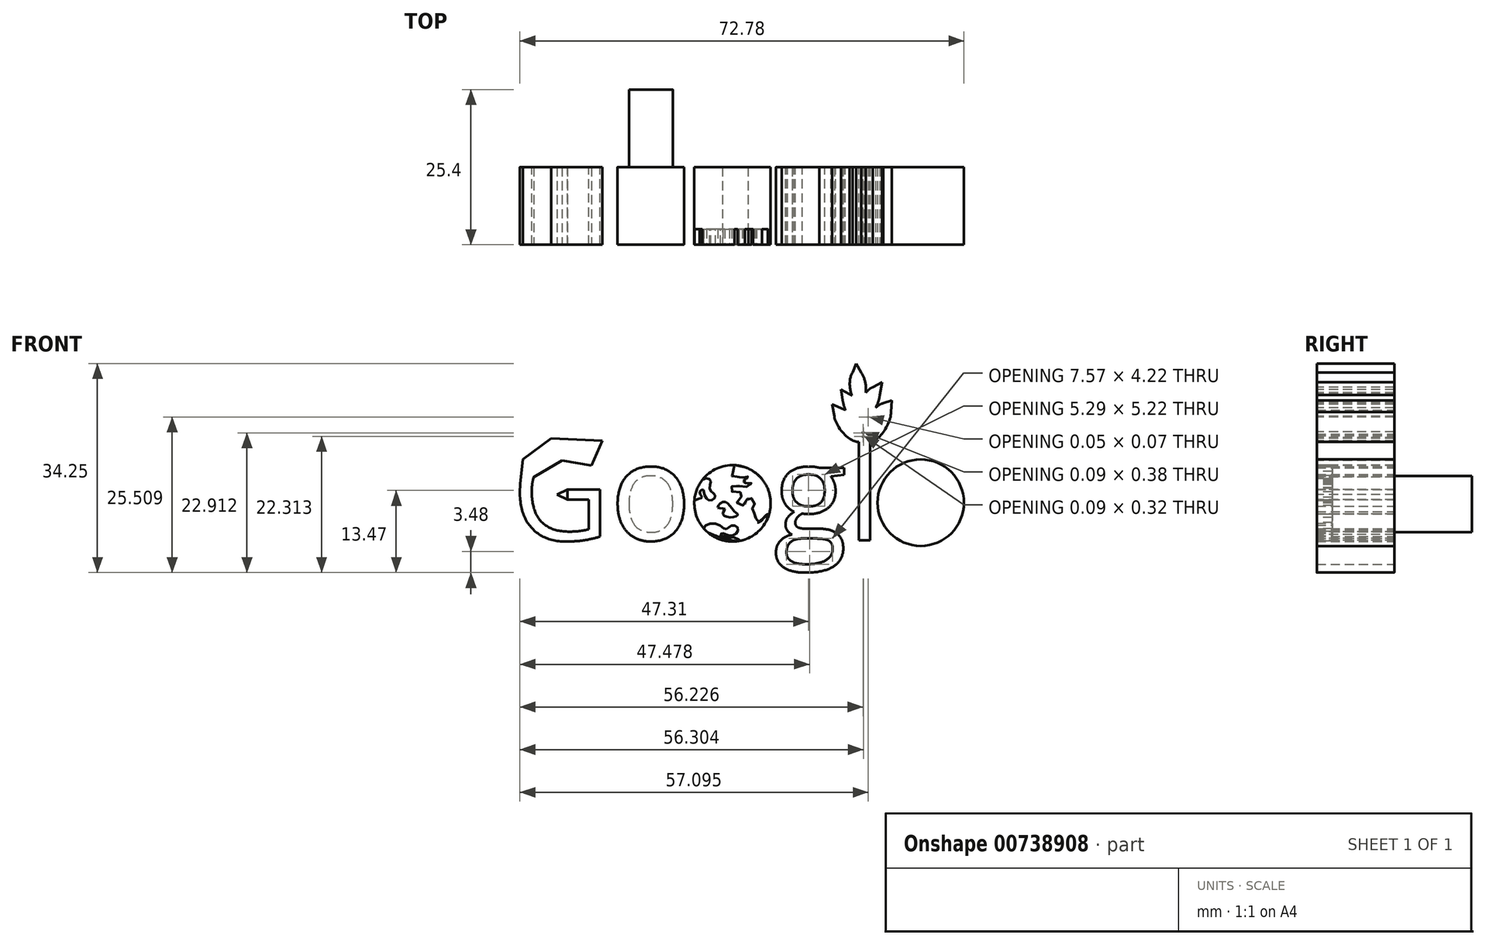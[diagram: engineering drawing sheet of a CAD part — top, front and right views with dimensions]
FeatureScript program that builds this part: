
annotation { "Feature Type Name" : "Feature", "Feature Type Description" : "" }
export const myFeature = defineFeature(function(context is Context, id is Id, definition is map)
    precondition{}
    {
        {
            var Q0;
            Q0=qCreatedBy(makeId("Front.planeOp"),FACE);
            var sketch = newSketch(context, id + "F0", { "sketchPlane" : qUnion([Q0])});
            skText(sketch, "E0", { "text": "Google", "fontName": "OpenSans-Regular.ttf"});
            const initialGuessF0  = {"E0": [-0.08015, -0.00937, 1, 0, 0.01595]};
            skSetInitialGuess(sketch, initialGuessF0);
            skSolve(sketch);
        }
        {
            var Q0;
            Q0 = qSketchRegion(id + "F0", true);
            extrude(context, id + "F1", {"entities" : qUnion([Q0]), "depth" : 12.7 * mm, "offsetDistance" : 25.4 * mm});
        }
        {
            var Q0;
            Q0=makeQuery(id+"F1.opExtrude","CAP_FACE",FACE,{"disambiguationData":[OSD([sQuery(id+"F0.wireOp",EDGE,"E0.sketch_text.stroke-0"),sQuery(id+"F0.wireOp",EDGE,"E0.sketch_text.stroke-1"),sQuery(id+"F0.wireOp",EDGE,"E0.sketch_text.stroke-2"),sQuery(id+"F0.wireOp",EDGE,"E0.sketch_text.stroke-3"),sQuery(id+"F0.wireOp",EDGE,"E0.sketch_text.stroke-4"),sQuery(id+"F0.wireOp",EDGE,"E0.sketch_text.stroke-5"),sQuery(id+"F0.wireOp",EDGE,"E0.sketch_text.stroke-6"),sQuery(id+"F0.wireOp",EDGE,"E0.sketch_text.stroke-7"),sQuery(id+"F0.wireOp",EDGE,"E0.sketch_text.stroke-8"),sQuery(id+"F0.wireOp",EDGE,"E0.sketch_text.stroke-9"),sQuery(id+"F0.wireOp",EDGE,"E0.sketch_text.stroke-10"),sQuery(id+"F0.wireOp",EDGE,"E0.sketch_text.stroke-11"),sQuery(id+"F0.wireOp",EDGE,"E0.sketch_text.stroke-12"),sQuery(id+"F0.wireOp",EDGE,"E0.sketch_text.stroke-13"),sQuery(id+"F0.wireOp",EDGE,"E0.sketch_text.stroke-14"),sQuery(id+"F0.wireOp",EDGE,"E0.sketch_text.stroke-15"),sQuery(id+"F0.wireOp",EDGE,"E0.sketch_text.stroke-16"),sQuery(id+"F0.wireOp",EDGE,"E0.sketch_text.stroke-17"),sQuery(id+"F0.wireOp",EDGE,"E0.sketch_text.stroke-18"),sQuery(id+"F0.wireOp",EDGE,"E0.sketch_text.stroke-19")])],"isStart":false});
            var sketch = newSketch(context, id + "F2", { "sketchPlane" : qUnion([Q0])});
            skLineSegment(sketch, "E1", {"start": v(-65.28, 6.96) * mm, "end": v(-67.07, 2.87) * mm});
            skLineSegment(sketch, "E2", {"start": v(-67.07, 2.87) * mm, "end": v(-74.25, 4.11) * mm});
            skLineSegment(sketch, "E3", {"start": v(-74.25, 4.11) * mm, "end": v(-67.07, 2.87) * mm});
            skLineSegment(sketch, "E4", {"start": v(-65.28, 6.96) * mm, "end": v(-73.65, 7.3) * mm});
            skLineSegment(sketch, "E5", {"start": v(-73.65, 7.3) * mm, "end": v(-78.28, 3.85) * mm});
            skLineSegment(sketch, "E6", {"start": v(-78.28, 3.85) * mm, "end": v(-78.74, -0.3) * mm});
            skLineSegment(sketch, "E7", {"start": v(-78.74, -0.3) * mm, "end": v(-71.88, 3.7) * mm});
            skSolve(sketch);
        }
        {
            var Q0;
            {var subQ5=sQuery(id+"F2.wireOp",EDGE,"E1");Q0=makeQuery(id+"F2.imprint","IMPRINT",FACE,{"disambiguationData":[TD([[makeQuery(id+"F2.imprint","IMPRINT",EDGE,{"derivedFrom":subQ5}),-1.0]])]});}
            extrude(context, id + "F3", {"entities" : qUnion([Q0]), "operationType" : NewBodyOperationType.ADD, "oppositeDirection" : true, "depth" : 12.7 * mm, "offsetDistance" : 25.4 * mm});
        }
        {
            var Q0;
            {var subQ0=sQuery(id+"F0.wireOp",EDGE,"E0.sketch_text.stroke-12");var subQ1=sQuery(id+"F0.wireOp",EDGE,"E0.sketch_text.stroke-11");var subQ2=sQuery(id+"F0.wireOp",EDGE,"E0.sketch_text.stroke-10");var subQ3=sQuery(id+"F0.wireOp",EDGE,"E0.sketch_text.stroke-9");var subQ4=sQuery(id+"F0.wireOp",EDGE,"E0.sketch_text.stroke-8");var subQ5=sQuery(id+"F0.wireOp",EDGE,"E0.sketch_text.stroke-7");var subQ6=sQuery(id+"F0.wireOp",EDGE,"E0.sketch_text.stroke-6");Q0=makeQuery(id+"F3.boolean.opBoolean","MERGE",FACE,{"derivedFrom":[makeQuery(id+"F1.opExtrude","CAP_FACE",FACE,{"disambiguationData":[OSD([sQuery(id+"F0.wireOp",EDGE,"E0.sketch_text.stroke-0"),sQuery(id+"F0.wireOp",EDGE,"E0.sketch_text.stroke-1"),sQuery(id+"F0.wireOp",EDGE,"E0.sketch_text.stroke-2"),sQuery(id+"F0.wireOp",EDGE,"E0.sketch_text.stroke-3"),sQuery(id+"F0.wireOp",EDGE,"E0.sketch_text.stroke-4"),sQuery(id+"F0.wireOp",EDGE,"E0.sketch_text.stroke-5"),subQ6,subQ5,subQ4,subQ3,subQ2,subQ1,subQ0,sQuery(id+"F0.wireOp",EDGE,"E0.sketch_text.stroke-13"),sQuery(id+"F0.wireOp",EDGE,"E0.sketch_text.stroke-14"),sQuery(id+"F0.wireOp",EDGE,"E0.sketch_text.stroke-15"),sQuery(id+"F0.wireOp",EDGE,"E0.sketch_text.stroke-16"),sQuery(id+"F0.wireOp",EDGE,"E0.sketch_text.stroke-17"),sQuery(id+"F0.wireOp",EDGE,"E0.sketch_text.stroke-18"),sQuery(id+"F0.wireOp",EDGE,"E0.sketch_text.stroke-19")])],"isStart":false}),makeQuery(id+"F3.opExtrude","CAP_FACE",FACE,{"disambiguationData":[OSD([subQ6,subQ5,subQ4,subQ3,subQ2,subQ1,subQ0,sQuery(id+"F2.wireOp",EDGE,"E1"),sQuery(id+"F2.wireOp",EDGE,"E3"),sQuery(id+"F2.wireOp",EDGE,"E4"),sQuery(id+"F2.wireOp",EDGE,"E5"),sQuery(id+"F2.wireOp",EDGE,"E6")])],"isStart":true})]});}
            var sketch = newSketch(context, id + "F4", { "sketchPlane" : qUnion([Q0])});
            skLineSegment(sketch, "E8", {"start": v(-71.02, -1.09) * mm, "end": v(-72.74, -1.9) * mm});
            skPoint(sketch, "E8.endSnap0", {"position": v(-71.02, -1.9) * mm});
            skLineSegment(sketch, "E9", {"start": v(-72.74, -1.9) * mm, "end": v(-71.02, -2.73) * mm});
            skLineSegment(sketch, "E10", {"start": v(-71.02, -2.73) * mm, "end": v(-71.02, -1.09) * mm});
            skSolve(sketch);
        }
        {
            var Q0;
            Q0=makeQuery(id+"F4.imprint","IMPRINT",FACE,{"disambiguationData":[TD([[makeQuery(id+"F4.imprint","IMPRINT",EDGE,{"derivedFrom":sQuery(id+"F4.wireOp",EDGE,"E8")}),1.0]])]});
            extrude(context, id + "F5", {"entities" : qUnion([Q0]), "operationType" : NewBodyOperationType.ADD, "oppositeDirection" : true, "depth" : 12.7 * mm, "offsetDistance" : 25.4 * mm});
        }
        {
            var Q0;
            Q0=makeQuery(id+"F1.opExtrude","CAP_FACE",FACE,{"disambiguationData":[OSD([sQuery(id+"F0.wireOp",EDGE,"E0.sketch_text.stroke-37"),sQuery(id+"F0.wireOp",EDGE,"E0.sketch_text.stroke-38"),sQuery(id+"F0.wireOp",EDGE,"E0.sketch_text.stroke-39"),sQuery(id+"F0.wireOp",EDGE,"E0.sketch_text.stroke-40"),sQuery(id+"F0.wireOp",EDGE,"E0.sketch_text.stroke-41"),sQuery(id+"F0.wireOp",EDGE,"E0.sketch_text.stroke-42"),sQuery(id+"F0.wireOp",EDGE,"E0.sketch_text.stroke-43"),sQuery(id+"F0.wireOp",EDGE,"E0.sketch_text.stroke-44"),sQuery(id+"F0.wireOp",EDGE,"E0.sketch_text.stroke-45"),sQuery(id+"F0.wireOp",EDGE,"E0.sketch_text.stroke-46"),sQuery(id+"F0.wireOp",EDGE,"E0.sketch_text.stroke-47"),sQuery(id+"F0.wireOp",EDGE,"E0.sketch_text.stroke-48"),sQuery(id+"F0.wireOp",EDGE,"E0.sketch_text.stroke-49"),sQuery(id+"F0.wireOp",EDGE,"E0.sketch_text.stroke-50"),sQuery(id+"F0.wireOp",EDGE,"E0.sketch_text.stroke-51"),sQuery(id+"F0.wireOp",EDGE,"E0.sketch_text.stroke-52"),sQuery(id+"F0.wireOp",EDGE,"E0.sketch_text.stroke-53")])],"isStart":false});
            var sketch = newSketch(context, id + "F6", { "sketchPlane" : qUnion([Q0])});
            skCircle(sketch, "E11", {"center": v(-43.96, -3.33) * mm, "radius": 6.26 * mm});
            skSolve(sketch);
        }
        {
            var Q0;
            {var subQ1=makeQuery(id+"F1.opExtrude","CAP_EDGE",EDGE,{"disambiguationData":[OSD([sQuery(id+"F0.wireOp",EDGE,"E0.sketch_text.stroke-37")])],"isStart":false});Q0=makeQuery(id+"F6.imprint","IMPRINT",FACE,{"disambiguationData":[TD([[makeQuery(id+"F6.imprint","IMPRINT",EDGE,{"derivedFrom":subQ1}),1.0]])]});}
            extrude(context, id + "F7", {"entities" : qUnion([Q0]), "operationType" : NewBodyOperationType.ADD, "oppositeDirection" : true, "depth" : 12.7 * mm, "offsetDistance" : 25.4 * mm});
        }
        {
            var Q0;
            {var subQ0=sQuery(id+"F0.wireOp",EDGE,"E0.sketch_text.stroke-45");var subQ1=sQuery(id+"F0.wireOp",EDGE,"E0.sketch_text.stroke-44");var subQ2=sQuery(id+"F0.wireOp",EDGE,"E0.sketch_text.stroke-43");var subQ3=sQuery(id+"F0.wireOp",EDGE,"E0.sketch_text.stroke-42");var subQ4=sQuery(id+"F0.wireOp",EDGE,"E0.sketch_text.stroke-41");var subQ5=sQuery(id+"F0.wireOp",EDGE,"E0.sketch_text.stroke-40");var subQ6=sQuery(id+"F0.wireOp",EDGE,"E0.sketch_text.stroke-39");var subQ7=sQuery(id+"F0.wireOp",EDGE,"E0.sketch_text.stroke-38");var subQ8=sQuery(id+"F0.wireOp",EDGE,"E0.sketch_text.stroke-37");Q0=makeQuery(id+"F7.boolean.opBoolean","MERGE",FACE,{"derivedFrom":[makeQuery(id+"F1.opExtrude","CAP_FACE",FACE,{"disambiguationData":[OSD([subQ8,subQ7,subQ6,subQ5,subQ4,subQ3,subQ2,subQ1,subQ0,sQuery(id+"F0.wireOp",EDGE,"E0.sketch_text.stroke-46"),sQuery(id+"F0.wireOp",EDGE,"E0.sketch_text.stroke-47"),sQuery(id+"F0.wireOp",EDGE,"E0.sketch_text.stroke-48"),sQuery(id+"F0.wireOp",EDGE,"E0.sketch_text.stroke-49"),sQuery(id+"F0.wireOp",EDGE,"E0.sketch_text.stroke-50"),sQuery(id+"F0.wireOp",EDGE,"E0.sketch_text.stroke-51"),sQuery(id+"F0.wireOp",EDGE,"E0.sketch_text.stroke-52"),sQuery(id+"F0.wireOp",EDGE,"E0.sketch_text.stroke-53")])],"isStart":false}),makeQuery(id+"F7.opExtrude","CAP_FACE",FACE,{"disambiguationData":[OSD([subQ8,subQ7,subQ6,subQ5,subQ4,subQ3,subQ2,subQ1,subQ0,sQuery(id+"F6.wireOp",EDGE,"E11")])],"isStart":true})]});}
            var sketch = newSketch(context, id + "F8", { "sketchPlane" : qUnion([Q0])});
            skCircle(sketch, "E12", {"center": v(-43.87, -3.43) * mm, "radius": 4.92 * mm});
            skPoint(sketch, "E12.first.point", {"position": v(-47.04, 0.32) * mm});
            skPoint(sketch, "E12.second.point", {"position": v(-40.87, -7.33) * mm});
            skPoint(sketch, "E12.third.point", {"position": v(-39.33, -1.54) * mm});
            skSolve(sketch);
        }
        {
            var Q0;
            Q0=makeQuery(id+"F8.imprint","IMPRINT",FACE,{"disambiguationData":[TD([[makeQuery(id+"F8.imprint","IMPRINT",EDGE,{"derivedFrom":makeQuery(id+"F1.opExtrude","CAP_EDGE",EDGE,{"disambiguationData":[OSD([sQuery(id+"F0.wireOp",EDGE,"E0.sketch_text.stroke-46")])],"isStart":false})}),1.0]])]});
            extrude(context, id + "F9", {"entities" : qUnion([Q0]), "operationType" : NewBodyOperationType.ADD, "oppositeDirection" : true, "depth" : 12.7 * mm, "offsetDistance" : 25.4 * mm});
        }
        {
            var Q0;
            {var subQ0=sQuery(id+"F0.wireOp",EDGE,"E0.sketch_text.stroke-53");var subQ1=sQuery(id+"F0.wireOp",EDGE,"E0.sketch_text.stroke-52");var subQ2=sQuery(id+"F0.wireOp",EDGE,"E0.sketch_text.stroke-51");var subQ3=sQuery(id+"F0.wireOp",EDGE,"E0.sketch_text.stroke-50");var subQ4=sQuery(id+"F0.wireOp",EDGE,"E0.sketch_text.stroke-49");var subQ5=sQuery(id+"F0.wireOp",EDGE,"E0.sketch_text.stroke-48");var subQ6=sQuery(id+"F0.wireOp",EDGE,"E0.sketch_text.stroke-47");var subQ7=sQuery(id+"F0.wireOp",EDGE,"E0.sketch_text.stroke-46");var subQ8=sQuery(id+"F0.wireOp",EDGE,"E0.sketch_text.stroke-45");var subQ9=sQuery(id+"F0.wireOp",EDGE,"E0.sketch_text.stroke-44");var subQ10=sQuery(id+"F0.wireOp",EDGE,"E0.sketch_text.stroke-43");var subQ11=sQuery(id+"F0.wireOp",EDGE,"E0.sketch_text.stroke-42");var subQ12=sQuery(id+"F0.wireOp",EDGE,"E0.sketch_text.stroke-41");var subQ13=sQuery(id+"F0.wireOp",EDGE,"E0.sketch_text.stroke-40");var subQ14=sQuery(id+"F0.wireOp",EDGE,"E0.sketch_text.stroke-39");var subQ15=sQuery(id+"F0.wireOp",EDGE,"E0.sketch_text.stroke-38");var subQ16=sQuery(id+"F0.wireOp",EDGE,"E0.sketch_text.stroke-37");Q0=makeQuery(id+"F9.boolean.opBoolean","MERGE",FACE,{"derivedFrom":[makeQuery(id+"F7.boolean.opBoolean","MERGE",FACE,{"derivedFrom":[makeQuery(id+"F1.opExtrude","CAP_FACE",FACE,{"disambiguationData":[OSD([subQ16,subQ15,subQ14,subQ13,subQ12,subQ11,subQ10,subQ9,subQ8,subQ7,subQ6,subQ5,subQ4,subQ3,subQ2,subQ1,subQ0])],"isStart":false}),makeQuery(id+"F7.opExtrude","CAP_FACE",FACE,{"disambiguationData":[OSD([subQ16,subQ15,subQ14,subQ13,subQ12,subQ11,subQ10,subQ9,subQ8,sQuery(id+"F6.wireOp",EDGE,"E11")])],"isStart":true})]}),makeQuery(id+"F9.opExtrude","CAP_FACE",FACE,{"disambiguationData":[OSD([subQ7,subQ6,subQ5,subQ4,subQ3,subQ2,subQ1,subQ0])],"isStart":true})]});}
            var sketch = newSketch(context, id + "F10", { "sketchPlane" : qUnion([Q0])});
            skFitSpline(sketch, "E13", {"points": [v(-43.63, 2.92) * mm, v(-43.9, 0.94) * mm, v(-41.88, 1.1) * mm, v(-41.53, 1.2) * mm, v(-41.38, 0.68) * mm, v(-42.16, 0.6) * mm, v(-42.2, 0) * mm, v(-41.22, 0.25) * mm, v(-40.87, -0.2) * mm, v(-41.41, -0.52) * mm, v(-42.6, -0.69) * mm, v(-43.3, -0.23) * mm, v(-44.46, -1.07) * mm, v(-43.9, -1.43) * mm, v(-42.7, -1.51) * mm, v(-42.39, -1.96) * mm, v(-42.59, -2.35) * mm, v(-43.23, -3.2) * mm, v(-42.77, -3.6) * mm, v(-41.71, -3.42) * mm, v(-41.51, -2.48) * mm, v(-40.96, -2.43) * mm, v(-40.39, -3.11) * mm, v(-40.36, -3.52) * mm, v(-40.74, -4.03) * mm, v(-40.61, -4.58) * mm, v(-40.48, -4.94) * mm, v(-40.02, -5.2) * mm, v(-40.2, -6.21) * mm, v(-39.7, -6.44) * mm, v(-38.94, -5.88) * mm, v(-38.28, -5.13) * mm, v(-37.97, -5.14) * mm, v(-37.7, -3.32) * mm, v(-38.2, -0.89) * mm, v(-39.1, 0.63) * mm, v(-40.57, 1.93) * mm, v(-41.94, 2.6) * mm, v(-43.1, 2.87) * mm, v(-43.63, 2.92) * mm]});
            skSolve(sketch);
        }
        {
            var Q0;
            {var subQ0=sQuery(id+"F10.wireOp",EDGE,"E13");var subQ1=makeQuery(id+"F7.opExtrude","CAP_EDGE",EDGE,{"disambiguationData":[OSD([sQuery(id+"F6.wireOp",EDGE,"E11")])],"isStart":true});var subQ7=makeQuery(id+"F10.imprint","INTERSECT",VERTEX,{"disambiguationData":[OD(0.0)],"derivedFrom":[subQ1,subQ0]});Q0=makeQuery(id+"F10.imprint","IMPRINT",FACE,{"disambiguationData":[TD([[makeQuery(id+"F10.imprint","IMPRINT",EDGE,{"disambiguationData":[TD([[subQ7,1.0]])],"derivedFrom":subQ0}),1.0]])]});}
            extrude(context, id + "F11", {"entities" : qUnion([Q0]), "operationType" : NewBodyOperationType.REMOVE, "oppositeDirection" : true, "depth" : 2.54 * mm, "offsetDistance" : 25.4 * mm});
        }
        {
            var Q0;
            {var subQ0=sQuery(id+"F0.wireOp",EDGE,"E0.sketch_text.stroke-38");var subQ2=sQuery(id+"F6.wireOp",EDGE,"E11");var subQ4=sQuery(id+"F0.wireOp",EDGE,"E0.sketch_text.stroke-39");var subQ5=sQuery(id+"F0.wireOp",EDGE,"E0.sketch_text.stroke-53");var subQ6=sQuery(id+"F0.wireOp",EDGE,"E0.sketch_text.stroke-52");var subQ7=sQuery(id+"F0.wireOp",EDGE,"E0.sketch_text.stroke-51");var subQ8=sQuery(id+"F0.wireOp",EDGE,"E0.sketch_text.stroke-50");var subQ9=sQuery(id+"F0.wireOp",EDGE,"E0.sketch_text.stroke-49");var subQ10=sQuery(id+"F0.wireOp",EDGE,"E0.sketch_text.stroke-48");var subQ11=sQuery(id+"F0.wireOp",EDGE,"E0.sketch_text.stroke-47");var subQ12=sQuery(id+"F0.wireOp",EDGE,"E0.sketch_text.stroke-46");var subQ13=sQuery(id+"F0.wireOp",EDGE,"E0.sketch_text.stroke-45");var subQ14=sQuery(id+"F0.wireOp",EDGE,"E0.sketch_text.stroke-44");var subQ15=sQuery(id+"F0.wireOp",EDGE,"E0.sketch_text.stroke-43");var subQ16=sQuery(id+"F0.wireOp",EDGE,"E0.sketch_text.stroke-42");var subQ17=sQuery(id+"F0.wireOp",EDGE,"E0.sketch_text.stroke-41");var subQ18=sQuery(id+"F0.wireOp",EDGE,"E0.sketch_text.stroke-40");var subQ19=sQuery(id+"F0.wireOp",EDGE,"E0.sketch_text.stroke-37");Q0=makeQuery(id+"F11.boolean.opBoolean","SPLIT",FACE,{"disambiguationData":[TD([makeQuery(id+"F1.opExtrude","SWEPT_FACE",FACE,{"disambiguationData":[OSD([subQ0])]})])],"derivedFrom":makeQuery(id+"F9.boolean.opBoolean","MERGE",FACE,{"derivedFrom":[makeQuery(id+"F7.boolean.opBoolean","MERGE",FACE,{"derivedFrom":[makeQuery(id+"F1.opExtrude","CAP_FACE",FACE,{"disambiguationData":[OSD([subQ19,subQ0,subQ4,subQ18,subQ17,subQ16,subQ15,subQ14,subQ13,subQ12,subQ11,subQ10,subQ9,subQ8,subQ7,subQ6,subQ5])],"isStart":false}),makeQuery(id+"F7.opExtrude","CAP_FACE",FACE,{"disambiguationData":[OSD([subQ19,subQ0,subQ4,subQ18,subQ17,subQ16,subQ15,subQ14,subQ13,subQ2])],"isStart":true})]}),makeQuery(id+"F9.opExtrude","CAP_FACE",FACE,{"disambiguationData":[OSD([subQ12,subQ11,subQ10,subQ9,subQ8,subQ7,subQ6,subQ5])],"isStart":true})]})});}
            var sketch = newSketch(context, id + "F12", { "sketchPlane" : qUnion([Q0])});
            skFitSpline(sketch, "E14", {"points": [v(-48.89, 0.52) * mm, v(-47.55, 0.43) * mm, v(-47.67, -1.09) * mm, v(-46.78, -2.06) * mm, v(-47.53, -2.87) * mm, v(-48.54, -1.94) * mm, v(-48.77, -1.1) * mm, v(-49.35, -1.52) * mm, v(-48.96, -2.35) * mm, v(-49.75, -2.66) * mm, v(-50.2, -2.8) * mm, v(-48.89, 0.52) * mm]});
            skSolve(sketch);
        }
        {
            var Q0;
            {var subQ0=sQuery(id+"F12.wireOp",EDGE,"E14");var subQ1=sQuery(id+"F6.wireOp",EDGE,"E11");var subQ8=sQuery(id+"F0.wireOp",EDGE,"E0.sketch_text.stroke-39");var subQ20=makeQuery(id+"F7.opExtrude","CAP_EDGE",EDGE,{"disambiguationData":[OSD([subQ1])],"isStart":true});var subQ21=makeQuery(id+"F11.boolean.opBoolean","SPLIT",EDGE,{"disambiguationData":[TD([makeQuery(id+"F1.opExtrude","SWEPT_FACE",FACE,{"disambiguationData":[OSD([subQ8])]})])],"derivedFrom":subQ20});var subQ22=makeQuery(id+"F12.imprint","INTERSECT",VERTEX,{"disambiguationData":[OD(0.0)],"derivedFrom":[subQ21,subQ0]});Q0=makeQuery(id+"F12.imprint","IMPRINT",FACE,{"disambiguationData":[TD([[makeQuery(id+"F12.imprint","IMPRINT",EDGE,{"disambiguationData":[TD([[subQ22,1.0]])],"derivedFrom":subQ0}),-1.0]])]});}
            extrude(context, id + "F13", {"entities" : qUnion([Q0]), "operationType" : NewBodyOperationType.REMOVE, "oppositeDirection" : true, "depth" : 2.54 * mm, "offsetDistance" : 25.4 * mm});
        }
        {
            var Q0;
            {var subQ0=sQuery(id+"F0.wireOp",EDGE,"E0.sketch_text.stroke-38");var subQ2=sQuery(id+"F6.wireOp",EDGE,"E11");var subQ4=sQuery(id+"F0.wireOp",EDGE,"E0.sketch_text.stroke-39");var subQ5=sQuery(id+"F0.wireOp",EDGE,"E0.sketch_text.stroke-53");var subQ6=sQuery(id+"F0.wireOp",EDGE,"E0.sketch_text.stroke-52");var subQ7=sQuery(id+"F0.wireOp",EDGE,"E0.sketch_text.stroke-51");var subQ8=sQuery(id+"F0.wireOp",EDGE,"E0.sketch_text.stroke-50");var subQ9=sQuery(id+"F0.wireOp",EDGE,"E0.sketch_text.stroke-49");var subQ10=sQuery(id+"F0.wireOp",EDGE,"E0.sketch_text.stroke-48");var subQ11=sQuery(id+"F0.wireOp",EDGE,"E0.sketch_text.stroke-47");var subQ12=sQuery(id+"F0.wireOp",EDGE,"E0.sketch_text.stroke-46");var subQ13=sQuery(id+"F0.wireOp",EDGE,"E0.sketch_text.stroke-45");var subQ14=sQuery(id+"F0.wireOp",EDGE,"E0.sketch_text.stroke-44");var subQ15=sQuery(id+"F0.wireOp",EDGE,"E0.sketch_text.stroke-43");var subQ16=sQuery(id+"F0.wireOp",EDGE,"E0.sketch_text.stroke-42");var subQ17=sQuery(id+"F0.wireOp",EDGE,"E0.sketch_text.stroke-41");var subQ18=sQuery(id+"F0.wireOp",EDGE,"E0.sketch_text.stroke-40");var subQ19=sQuery(id+"F0.wireOp",EDGE,"E0.sketch_text.stroke-37");Q0=makeQuery(id+"F11.boolean.opBoolean","SPLIT",FACE,{"disambiguationData":[TD([makeQuery(id+"F1.opExtrude","SWEPT_FACE",FACE,{"disambiguationData":[OSD([subQ0])]})])],"derivedFrom":makeQuery(id+"F9.boolean.opBoolean","MERGE",FACE,{"derivedFrom":[makeQuery(id+"F7.boolean.opBoolean","MERGE",FACE,{"derivedFrom":[makeQuery(id+"F1.opExtrude","CAP_FACE",FACE,{"disambiguationData":[OSD([subQ19,subQ0,subQ4,subQ18,subQ17,subQ16,subQ15,subQ14,subQ13,subQ12,subQ11,subQ10,subQ9,subQ8,subQ7,subQ6,subQ5])],"isStart":false}),makeQuery(id+"F7.opExtrude","CAP_FACE",FACE,{"disambiguationData":[OSD([subQ19,subQ0,subQ4,subQ18,subQ17,subQ16,subQ15,subQ14,subQ13,subQ2])],"isStart":true})]}),makeQuery(id+"F9.opExtrude","CAP_FACE",FACE,{"disambiguationData":[OSD([subQ12,subQ11,subQ10,subQ9,subQ8,subQ7,subQ6,subQ5])],"isStart":true})]})});}
            var sketch = newSketch(context, id + "F14", { "sketchPlane" : qUnion([Q0])});
            skFitSpline(sketch, "E15", {"points": [v(-46.34, -4.03) * mm, v(-45.35, -3.06) * mm, v(-43.81, -4.47) * mm, v(-43.1, -5.2) * mm, v(-44.15, -5.63) * mm, v(-45.54, -5.03) * mm, v(-45.22, -4.24) * mm, v(-46.34, -4.03) * mm]});
            skSolve(sketch);
        }
        {
            var Q0;
            Q0=makeQuery(id+"F14.imprint","IMPRINT",FACE,{"disambiguationData":[TD([[makeQuery(id+"F14.imprint","IMPRINT",EDGE,{"derivedFrom":sQuery(id+"F14.wireOp",EDGE,"E15")}),-1.0]])]});
            extrude(context, id + "F15", {"entities" : qUnion([Q0]), "operationType" : NewBodyOperationType.REMOVE, "oppositeDirection" : true, "depth" : 2.54 * mm, "offsetDistance" : 25.4 * mm});
        }
        {
            var Q0;
            {var subQ0=sQuery(id+"F0.wireOp",EDGE,"E0.sketch_text.stroke-38");var subQ2=sQuery(id+"F6.wireOp",EDGE,"E11");var subQ4=sQuery(id+"F0.wireOp",EDGE,"E0.sketch_text.stroke-39");var subQ5=sQuery(id+"F0.wireOp",EDGE,"E0.sketch_text.stroke-53");var subQ6=sQuery(id+"F0.wireOp",EDGE,"E0.sketch_text.stroke-52");var subQ7=sQuery(id+"F0.wireOp",EDGE,"E0.sketch_text.stroke-51");var subQ8=sQuery(id+"F0.wireOp",EDGE,"E0.sketch_text.stroke-50");var subQ9=sQuery(id+"F0.wireOp",EDGE,"E0.sketch_text.stroke-49");var subQ10=sQuery(id+"F0.wireOp",EDGE,"E0.sketch_text.stroke-48");var subQ11=sQuery(id+"F0.wireOp",EDGE,"E0.sketch_text.stroke-47");var subQ12=sQuery(id+"F0.wireOp",EDGE,"E0.sketch_text.stroke-46");var subQ13=sQuery(id+"F0.wireOp",EDGE,"E0.sketch_text.stroke-45");var subQ14=sQuery(id+"F0.wireOp",EDGE,"E0.sketch_text.stroke-44");var subQ15=sQuery(id+"F0.wireOp",EDGE,"E0.sketch_text.stroke-43");var subQ16=sQuery(id+"F0.wireOp",EDGE,"E0.sketch_text.stroke-42");var subQ17=sQuery(id+"F0.wireOp",EDGE,"E0.sketch_text.stroke-41");var subQ18=sQuery(id+"F0.wireOp",EDGE,"E0.sketch_text.stroke-40");var subQ19=sQuery(id+"F0.wireOp",EDGE,"E0.sketch_text.stroke-37");Q0=makeQuery(id+"F11.boolean.opBoolean","SPLIT",FACE,{"disambiguationData":[TD([makeQuery(id+"F1.opExtrude","SWEPT_FACE",FACE,{"disambiguationData":[OSD([subQ0])]})])],"derivedFrom":makeQuery(id+"F9.boolean.opBoolean","MERGE",FACE,{"derivedFrom":[makeQuery(id+"F7.boolean.opBoolean","MERGE",FACE,{"derivedFrom":[makeQuery(id+"F1.opExtrude","CAP_FACE",FACE,{"disambiguationData":[OSD([subQ19,subQ0,subQ4,subQ18,subQ17,subQ16,subQ15,subQ14,subQ13,subQ12,subQ11,subQ10,subQ9,subQ8,subQ7,subQ6,subQ5])],"isStart":false}),makeQuery(id+"F7.opExtrude","CAP_FACE",FACE,{"disambiguationData":[OSD([subQ19,subQ0,subQ4,subQ18,subQ17,subQ16,subQ15,subQ14,subQ13,subQ2])],"isStart":true})]}),makeQuery(id+"F9.opExtrude","CAP_FACE",FACE,{"disambiguationData":[OSD([subQ12,subQ11,subQ10,subQ9,subQ8,subQ7,subQ6,subQ5])],"isStart":true})]})});}
            var sketch = newSketch(context, id + "F16", { "sketchPlane" : qUnion([Q0])});
            skFitSpline(sketch, "E16", {"points": [v(-48.62, -7.51) * mm, v(-46.76, -6.63) * mm, v(-45.06, -7.56) * mm, v(-44.1, -6.96) * mm, v(-43.07, -7.4) * mm, v(-43.54, -8.43) * mm, v(-44.96, -8.5) * mm, v(-45.7, -8.24) * mm, v(-45.86, -8.6) * mm, v(-43.48, -9.01) * mm, v(-42.85, -9.5) * mm, v(-48.62, -7.51) * mm]});
            skSolve(sketch);
        }
        {
            var Q0;
            {var subQ0=sQuery(id+"F16.wireOp",EDGE,"E16");var subQ1=sQuery(id+"F0.wireOp",EDGE,"E0.sketch_text.stroke-38");var subQ2=makeQuery(id+"F1.opExtrude","CAP_EDGE",EDGE,{"disambiguationData":[OSD([subQ1])],"isStart":false});var subQ3=makeQuery(id+"F16.imprint","INTERSECT",VERTEX,{"disambiguationData":[OD(0.0)],"derivedFrom":[subQ2,subQ0]});Q0=makeQuery(id+"F16.imprint","IMPRINT",FACE,{"disambiguationData":[TD([[makeQuery(id+"F16.imprint","IMPRINT",EDGE,{"disambiguationData":[TD([[subQ3,-1.0]])],"derivedFrom":subQ2}),-1.0]])]});}
            extrude(context, id + "F17", {"entities" : qUnion([Q0]), "operationType" : NewBodyOperationType.REMOVE, "oppositeDirection" : true, "depth" : 2.54 * mm, "offsetDistance" : 25.4 * mm});
        }
        {
            var Q0;
            Q0=makeQuery(id+"F1.opExtrude","CAP_FACE",FACE,{"disambiguationData":[OSD([sQuery(id+"F0.wireOp",EDGE,"E0.sketch_text.stroke-20"),sQuery(id+"F0.wireOp",EDGE,"E0.sketch_text.stroke-21"),sQuery(id+"F0.wireOp",EDGE,"E0.sketch_text.stroke-22"),sQuery(id+"F0.wireOp",EDGE,"E0.sketch_text.stroke-23"),sQuery(id+"F0.wireOp",EDGE,"E0.sketch_text.stroke-24"),sQuery(id+"F0.wireOp",EDGE,"E0.sketch_text.stroke-25"),sQuery(id+"F0.wireOp",EDGE,"E0.sketch_text.stroke-26"),sQuery(id+"F0.wireOp",EDGE,"E0.sketch_text.stroke-27"),sQuery(id+"F0.wireOp",EDGE,"E0.sketch_text.stroke-28"),sQuery(id+"F0.wireOp",EDGE,"E0.sketch_text.stroke-29"),sQuery(id+"F0.wireOp",EDGE,"E0.sketch_text.stroke-30"),sQuery(id+"F0.wireOp",EDGE,"E0.sketch_text.stroke-31"),sQuery(id+"F0.wireOp",EDGE,"E0.sketch_text.stroke-32"),sQuery(id+"F0.wireOp",EDGE,"E0.sketch_text.stroke-33"),sQuery(id+"F0.wireOp",EDGE,"E0.sketch_text.stroke-34"),sQuery(id+"F0.wireOp",EDGE,"E0.sketch_text.stroke-35"),sQuery(id+"F0.wireOp",EDGE,"E0.sketch_text.stroke-36")])],"isStart":false});
            var sketch = newSketch(context, id + "F18", { "sketchPlane" : qUnion([Q0])});
            skCircle(sketch, "E17", {"center": v(-57.35, -3.38) * mm, "radius": 6.42 * mm});
            skSolve(sketch);
        }
        {
            var Q0;
            Q0=makeQuery(id+"F18.imprint","IMPRINT",FACE,{"disambiguationData":[TD([[makeQuery(id+"F18.imprint","IMPRINT",EDGE,{"derivedFrom":makeQuery(id+"F1.opExtrude","CAP_EDGE",EDGE,{"disambiguationData":[OSD([sQuery(id+"F0.wireOp",EDGE,"E0.sketch_text.stroke-29")])],"isStart":false})}),1.0]])]});
            extrude(context, id + "F19", {"entities" : qUnion([Q0]), "oppositeDirection" : true, "depth" : 25.4 * mm, "offsetDistance" : 25.4 * mm});
        }
        {
            var Q0;
            Q0=makeQuery(id+"F1.opExtrude","CAP_FACE",FACE,{"disambiguationData":[OSD([sQuery(id+"F0.wireOp",EDGE,"E0.sketch_text.stroke-98"),sQuery(id+"F0.wireOp",EDGE,"E0.sketch_text.stroke-99"),sQuery(id+"F0.wireOp",EDGE,"E0.sketch_text.stroke-100"),sQuery(id+"F0.wireOp",EDGE,"E0.sketch_text.stroke-101")])],"isStart":false});
            var sketch = newSketch(context, id + "F20", { "sketchPlane" : qUnion([Q0])});
            skEllipse(sketch, "E18", {"center": v(-24.91, 9.5) * mm, "majorRadius": 3.32 * mm, "minorRadius": 1.54 * mm, "majorAxis": v(0.62, -0.78)});
            skSolve(sketch);
        }
        {
            var Q0;
            {var subQ0=sQuery(id+"F20.wireOp",EDGE,"E18");var subQ1=makeQuery(id+"F1.opExtrude","CAP_EDGE",EDGE,{"disambiguationData":[OSD([sQuery(id+"F0.wireOp",EDGE,"E0.sketch_text.stroke-99")])],"isStart":false});var subQ2=makeQuery(id+"F20.imprint","INTERSECT",VERTEX,{"derivedFrom":[subQ1,subQ0]});Q0=makeQuery(id+"F20.imprint","IMPRINT",FACE,{"disambiguationData":[TD([[makeQuery(id+"F20.imprint","IMPRINT",EDGE,{"disambiguationData":[TD([[subQ2,1.0]])],"derivedFrom":subQ0}),1.0]])]});}
            extrude(context, id + "F21", {"entities" : qUnion([Q0]), "operationType" : NewBodyOperationType.ADD, "oppositeDirection" : true, "depth" : 12.7 * mm, "offsetDistance" : 25.4 * mm});
        }
        {
            var Q0;
            {var subQ0=sQuery(id+"F0.wireOp",EDGE,"E0.sketch_text.stroke-100");var subQ1=sQuery(id+"F0.wireOp",EDGE,"E0.sketch_text.stroke-99");Q0=makeQuery(id+"F21.boolean.opBoolean","MERGE",FACE,{"derivedFrom":[makeQuery(id+"F1.opExtrude","CAP_FACE",FACE,{"disambiguationData":[OSD([sQuery(id+"F0.wireOp",EDGE,"E0.sketch_text.stroke-98"),subQ1,subQ0,sQuery(id+"F0.wireOp",EDGE,"E0.sketch_text.stroke-101")])],"isStart":false}),makeQuery(id+"F21.opExtrude","CAP_FACE",FACE,{"disambiguationData":[OSD([subQ1,subQ0,sQuery(id+"F20.wireOp",EDGE,"E18")])],"isStart":true})]});}
            var sketch = newSketch(context, id + "F22", { "sketchPlane" : qUnion([Q0])});
            skEllipse(sketch, "E19", {"center": v(-20.25, 9.92) * mm, "majorRadius": 3.54 * mm, "minorRadius": 1.7 * mm, "majorAxis": v(-0.5, -0.87)});
            skSolve(sketch);
        }
        {
            var Q0;
            {var subQ3=sQuery(id+"F22.wireOp",EDGE,"E19");var subQ5=makeQuery(id+"F21.opExtrude","CAP_EDGE",EDGE,{"disambiguationData":[OSD([sQuery(id+"F20.wireOp",EDGE,"E18")])],"isStart":true});var subQ8=makeQuery(id+"F22.imprint","INTERSECT",VERTEX,{"disambiguationData":[OD(0.0)],"derivedFrom":[subQ5,subQ3]});Q0=makeQuery(id+"F22.imprint","IMPRINT",FACE,{"disambiguationData":[TD([[makeQuery(id+"F22.imprint","IMPRINT",EDGE,{"disambiguationData":[TD([[subQ8,1.0]])],"derivedFrom":subQ3}),1.0]])]});}
            extrude(context, id + "F23", {"entities" : qUnion([Q0]), "operationType" : NewBodyOperationType.ADD, "oppositeDirection" : true, "depth" : 12.7 * mm, "offsetDistance" : 25.4 * mm});
        }
        {
            var Q0;
            {var subQ0=sQuery(id+"F20.wireOp",EDGE,"E18");var subQ1=sQuery(id+"F0.wireOp",EDGE,"E0.sketch_text.stroke-101");var subQ2=sQuery(id+"F0.wireOp",EDGE,"E0.sketch_text.stroke-100");var subQ3=sQuery(id+"F0.wireOp",EDGE,"E0.sketch_text.stroke-99");Q0=makeQuery(id+"F23.boolean.opBoolean","MERGE",FACE,{"derivedFrom":[makeQuery(id+"F21.boolean.opBoolean","MERGE",FACE,{"derivedFrom":[makeQuery(id+"F1.opExtrude","CAP_FACE",FACE,{"disambiguationData":[OSD([sQuery(id+"F0.wireOp",EDGE,"E0.sketch_text.stroke-98"),subQ3,subQ2,subQ1])],"isStart":false}),makeQuery(id+"F21.opExtrude","CAP_FACE",FACE,{"disambiguationData":[OSD([subQ3,subQ2,subQ0])],"isStart":true})]}),makeQuery(id+"F23.opExtrude","CAP_FACE",FACE,{"disambiguationData":[OSD([subQ2,subQ1,subQ0,sQuery(id+"F22.wireOp",EDGE,"E19")])],"isStart":true})]});}
            var sketch = newSketch(context, id + "F24", { "sketchPlane" : qUnion([Q0])});
            skEllipse(sketch, "E20", {"center": v(-23.6, 11.44) * mm, "majorRadius": 3.65 * mm, "minorRadius": 1.4 * mm, "majorAxis": v(0.52, -0.85)});
            skSolve(sketch);
        }
        {
            var Q0;
            {var subQ0=sQuery(id+"F24.wireOp",EDGE,"E20");var subQ1=sQuery(id+"F20.wireOp",EDGE,"E18");var subQ5=sQuery(id+"F22.wireOp",EDGE,"E19");var subQ6=makeQuery(id+"F21.opExtrude","CAP_EDGE",EDGE,{"disambiguationData":[OSD([subQ1])],"isStart":true});var subQ7=makeQuery(id+"F22.imprint","IMPRINT",EDGE,{"disambiguationData":[TD([[makeQuery(id+"F22.imprint","INTERSECT",VERTEX,{"disambiguationData":[OD(0.0)],"derivedFrom":[subQ6,subQ5]}),1.0]])],"derivedFrom":subQ5});var subQ10=makeQuery(id+"F23.opExtrude","CAP_EDGE",EDGE,{"disambiguationData":[OSD([subQ5]),TDD([subQ7])],"isStart":true});var subQ11=makeQuery(id+"F24.imprint","INTERSECT",VERTEX,{"disambiguationData":[OD(0.0)],"derivedFrom":[subQ10,subQ0]});Q0=makeQuery(id+"F24.imprint","IMPRINT",FACE,{"disambiguationData":[TD([[makeQuery(id+"F24.imprint","IMPRINT",EDGE,{"disambiguationData":[TD([[subQ11,-1.0]])],"derivedFrom":subQ10}),-1.0]])]});}
            extrude(context, id + "F25", {"entities" : qUnion([Q0]), "operationType" : NewBodyOperationType.ADD, "oppositeDirection" : true, "depth" : 12.7 * mm, "offsetDistance" : 25.4 * mm});
        }
        {
            var Q0;
            {var subQ0=sQuery(id+"F22.wireOp",EDGE,"E19");var subQ1=sQuery(id+"F20.wireOp",EDGE,"E18");var subQ2=sQuery(id+"F0.wireOp",EDGE,"E0.sketch_text.stroke-101");var subQ3=sQuery(id+"F0.wireOp",EDGE,"E0.sketch_text.stroke-100");var subQ4=sQuery(id+"F0.wireOp",EDGE,"E0.sketch_text.stroke-99");Q0=makeQuery(id+"F25.boolean.opBoolean","MERGE",FACE,{"derivedFrom":[makeQuery(id+"F23.boolean.opBoolean","MERGE",FACE,{"derivedFrom":[makeQuery(id+"F21.boolean.opBoolean","MERGE",FACE,{"derivedFrom":[makeQuery(id+"F1.opExtrude","CAP_FACE",FACE,{"disambiguationData":[OSD([sQuery(id+"F0.wireOp",EDGE,"E0.sketch_text.stroke-98"),subQ4,subQ3,subQ2])],"isStart":false}),makeQuery(id+"F21.opExtrude","CAP_FACE",FACE,{"disambiguationData":[OSD([subQ4,subQ3,subQ1])],"isStart":true})]}),makeQuery(id+"F23.opExtrude","CAP_FACE",FACE,{"disambiguationData":[OSD([subQ3,subQ2,subQ1,subQ0])],"isStart":true})]}),makeQuery(id+"F25.opExtrude","CAP_FACE",FACE,{"disambiguationData":[OSD([subQ1,subQ0,sQuery(id+"F24.wireOp",EDGE,"E20")])],"isStart":true})]});}
            var sketch = newSketch(context, id + "F26", { "sketchPlane" : qUnion([Q0])});
            skEllipse(sketch, "E21", {"center": v(-21.66, 13.07) * mm, "majorRadius": 2.98 * mm, "minorRadius": 1.36 * mm, "majorAxis": v(-0.47, -0.88)});
            skSolve(sketch);
        }
        {
            var Q0;
            {var subQ0=sQuery(id+"F26.wireOp",EDGE,"E21");var subQ1=sQuery(id+"F22.wireOp",EDGE,"E19");var subQ2=sQuery(id+"F20.wireOp",EDGE,"E18");var subQ3=makeQuery(id+"F21.opExtrude","CAP_EDGE",EDGE,{"disambiguationData":[OSD([subQ2])],"isStart":true});var subQ5=makeQuery(id+"F22.imprint","IMPRINT",EDGE,{"disambiguationData":[TD([[makeQuery(id+"F22.imprint","INTERSECT",VERTEX,{"disambiguationData":[OD(0.0)],"derivedFrom":[subQ3,subQ1]}),1.0]])],"derivedFrom":subQ1});var subQ11=sQuery(id+"F24.wireOp",EDGE,"E20");var subQ13=makeQuery(id+"F23.opExtrude","CAP_EDGE",EDGE,{"disambiguationData":[OSD([subQ1]),TDD([subQ5])],"isStart":true});var subQ14=makeQuery(id+"F24.imprint","IMPRINT",EDGE,{"disambiguationData":[TD([[makeQuery(id+"F24.imprint","INTERSECT",VERTEX,{"disambiguationData":[OD(0.0)],"derivedFrom":[subQ13,subQ11]}),-1.0]])],"derivedFrom":subQ11});var subQ17=makeQuery(id+"F25.opExtrude","CAP_EDGE",EDGE,{"disambiguationData":[OSD([subQ11]),TDD([subQ14])],"isStart":true});var subQ20=makeQuery(id+"F26.imprint","INTERSECT",VERTEX,{"disambiguationData":[OD(0.0)],"derivedFrom":[subQ17,subQ0]});Q0=makeQuery(id+"F26.imprint","IMPRINT",FACE,{"disambiguationData":[TD([[makeQuery(id+"F26.imprint","IMPRINT",EDGE,{"disambiguationData":[TD([[subQ20,1.0]])],"derivedFrom":subQ17}),-1.0]])]});}
            extrude(context, id + "F27", {"entities" : qUnion([Q0]), "operationType" : NewBodyOperationType.ADD, "oppositeDirection" : true, "depth" : 12.7 * mm, "offsetDistance" : 25.4 * mm});
        }
        {
            var Q0;
            {var subQ0=sQuery(id+"F24.wireOp",EDGE,"E20");var subQ1=sQuery(id+"F22.wireOp",EDGE,"E19");var subQ2=sQuery(id+"F20.wireOp",EDGE,"E18");var subQ3=sQuery(id+"F0.wireOp",EDGE,"E0.sketch_text.stroke-101");var subQ4=sQuery(id+"F0.wireOp",EDGE,"E0.sketch_text.stroke-100");var subQ5=sQuery(id+"F0.wireOp",EDGE,"E0.sketch_text.stroke-99");Q0=makeQuery(id+"F27.boolean.opBoolean","MERGE",FACE,{"derivedFrom":[makeQuery(id+"F25.boolean.opBoolean","MERGE",FACE,{"derivedFrom":[makeQuery(id+"F23.boolean.opBoolean","MERGE",FACE,{"derivedFrom":[makeQuery(id+"F21.boolean.opBoolean","MERGE",FACE,{"derivedFrom":[makeQuery(id+"F1.opExtrude","CAP_FACE",FACE,{"disambiguationData":[OSD([sQuery(id+"F0.wireOp",EDGE,"E0.sketch_text.stroke-98"),subQ5,subQ4,subQ3])],"isStart":false}),makeQuery(id+"F21.opExtrude","CAP_FACE",FACE,{"disambiguationData":[OSD([subQ5,subQ4,subQ2])],"isStart":true})]}),makeQuery(id+"F23.opExtrude","CAP_FACE",FACE,{"disambiguationData":[OSD([subQ4,subQ3,subQ2,subQ1])],"isStart":true})]}),makeQuery(id+"F25.opExtrude","CAP_FACE",FACE,{"disambiguationData":[OSD([subQ2,subQ1,subQ0])],"isStart":true})]}),makeQuery(id+"F27.opExtrude","CAP_FACE",FACE,{"disambiguationData":[OSD([subQ1,subQ0,sQuery(id+"F26.wireOp",EDGE,"E21")])],"isStart":true})]});}
            var sketch = newSketch(context, id + "F28", { "sketchPlane" : qUnion([Q0])});
            skEllipse(sketch, "E22", {"center": v(-23.4, 15.82) * mm, "majorRadius": 2.68 * mm, "minorRadius": 1.3 * mm, "majorAxis": v(0.1, -1)});
            skSolve(sketch);
        }
        {
            var Q0;
            {var subQ0=sQuery(id+"F28.wireOp",EDGE,"E22");var subQ1=sQuery(id+"F26.wireOp",EDGE,"E21");var subQ2=sQuery(id+"F22.wireOp",EDGE,"E19");var subQ3=sQuery(id+"F20.wireOp",EDGE,"E18");var subQ4=makeQuery(id+"F21.opExtrude","CAP_EDGE",EDGE,{"disambiguationData":[OSD([subQ3])],"isStart":true});var subQ6=makeQuery(id+"F22.imprint","IMPRINT",EDGE,{"disambiguationData":[TD([[makeQuery(id+"F22.imprint","INTERSECT",VERTEX,{"disambiguationData":[OD(0.0)],"derivedFrom":[subQ4,subQ2]}),1.0]])],"derivedFrom":subQ2});var subQ12=sQuery(id+"F24.wireOp",EDGE,"E20");var subQ16=makeQuery(id+"F23.opExtrude","CAP_EDGE",EDGE,{"disambiguationData":[OSD([subQ2]),TDD([subQ6])],"isStart":true});var subQ17=makeQuery(id+"F24.imprint","IMPRINT",EDGE,{"disambiguationData":[TD([[makeQuery(id+"F24.imprint","INTERSECT",VERTEX,{"disambiguationData":[OD(0.0)],"derivedFrom":[subQ16,subQ12]}),-1.0]])],"derivedFrom":subQ12});var subQ19=makeQuery(id+"F25.opExtrude","CAP_EDGE",EDGE,{"disambiguationData":[OSD([subQ12]),TDD([subQ17])],"isStart":true});var subQ20=makeQuery(id+"F26.imprint","IMPRINT",EDGE,{"disambiguationData":[TD([[makeQuery(id+"F26.imprint","INTERSECT",VERTEX,{"disambiguationData":[OD(0.0)],"derivedFrom":[subQ19,subQ1]}),1.0]])],"derivedFrom":subQ1});var subQ21=makeQuery(id+"F27.opExtrude","CAP_EDGE",EDGE,{"disambiguationData":[OSD([subQ1]),TDD([subQ20])],"isStart":true});var subQ22=makeQuery(id+"F28.imprint","INTERSECT",VERTEX,{"derivedFrom":[subQ21,subQ0]});Q0=makeQuery(id+"F28.imprint","IMPRINT",FACE,{"disambiguationData":[TD([[makeQuery(id+"F28.imprint","IMPRINT",EDGE,{"disambiguationData":[TD([[subQ22,-1.0]])],"derivedFrom":subQ0}),1.0]])]});}
            extrude(context, id + "F29", {"entities" : qUnion([Q0]), "operationType" : NewBodyOperationType.ADD, "oppositeDirection" : true, "depth" : 12.7 * mm, "offsetDistance" : 25.4 * mm});
        }
        {
            var Q0;
            {var subQ0=sQuery(id+"F26.wireOp",EDGE,"E21");var subQ1=sQuery(id+"F24.wireOp",EDGE,"E20");var subQ2=sQuery(id+"F22.wireOp",EDGE,"E19");var subQ3=sQuery(id+"F20.wireOp",EDGE,"E18");var subQ4=sQuery(id+"F0.wireOp",EDGE,"E0.sketch_text.stroke-101");var subQ5=sQuery(id+"F0.wireOp",EDGE,"E0.sketch_text.stroke-100");var subQ6=sQuery(id+"F0.wireOp",EDGE,"E0.sketch_text.stroke-99");Q0=makeQuery(id+"F29.boolean.opBoolean","MERGE",FACE,{"derivedFrom":[makeQuery(id+"F27.boolean.opBoolean","MERGE",FACE,{"derivedFrom":[makeQuery(id+"F25.boolean.opBoolean","MERGE",FACE,{"derivedFrom":[makeQuery(id+"F23.boolean.opBoolean","MERGE",FACE,{"derivedFrom":[makeQuery(id+"F21.boolean.opBoolean","MERGE",FACE,{"derivedFrom":[makeQuery(id+"F1.opExtrude","CAP_FACE",FACE,{"disambiguationData":[OSD([sQuery(id+"F0.wireOp",EDGE,"E0.sketch_text.stroke-98"),subQ6,subQ5,subQ4])],"isStart":false}),makeQuery(id+"F21.opExtrude","CAP_FACE",FACE,{"disambiguationData":[OSD([subQ6,subQ5,subQ3])],"isStart":true})]}),makeQuery(id+"F23.opExtrude","CAP_FACE",FACE,{"disambiguationData":[OSD([subQ5,subQ4,subQ3,subQ2])],"isStart":true})]}),makeQuery(id+"F25.opExtrude","CAP_FACE",FACE,{"disambiguationData":[OSD([subQ3,subQ2,subQ1])],"isStart":true})]}),makeQuery(id+"F27.opExtrude","CAP_FACE",FACE,{"disambiguationData":[OSD([subQ2,subQ1,subQ0])],"isStart":true})]}),makeQuery(id+"F29.opExtrude","CAP_FACE",FACE,{"disambiguationData":[OSD([subQ1,subQ0,sQuery(id+"F28.wireOp",EDGE,"E22")])],"isStart":true})]});}
            var sketch = newSketch(context, id + "F30", { "sketchPlane" : qUnion([Q0])});
            skLineSegment(sketch, "E23", {"start": v(-23.7, 19.56) * mm, "end": v(-24.68, 17.06) * mm});
            skPoint(sketch, "E23.startSnap0", {"position": v(-23.7, 18.48) * mm});
            skLineSegment(sketch, "E24", {"start": v(-24.68, 17.06) * mm, "end": v(-22.35, 17.06) * mm});
            skLineSegment(sketch, "E25", {"start": v(-22.35, 17.06) * mm, "end": v(-23.7, 19.56) * mm});
            skSolve(sketch);
        }
        {
            var Q0;
            {var subQ0=sQuery(id+"F30.wireOp",EDGE,"E25");var subQ1=sQuery(id+"F30.wireOp",EDGE,"E23");var subQ2=makeQuery(id+"F30.imprint","INTERSECT",VERTEX,{"derivedFrom":[subQ1,subQ0]});Q0=makeQuery(id+"F30.imprint","IMPRINT",FACE,{"disambiguationData":[TD([[makeQuery(id+"F30.imprint","IMPRINT",EDGE,{"disambiguationData":[TD([[subQ2,-1.0]])],"derivedFrom":subQ1}),1.0]])]});}
            extrude(context, id + "F31", {"entities" : qUnion([Q0]), "operationType" : NewBodyOperationType.ADD, "oppositeDirection" : true, "depth" : 12.7 * mm, "offsetDistance" : 25.4 * mm});
        }
        {
            var Q0;
            {var subQ0=sQuery(id+"F28.wireOp",EDGE,"E22");var subQ1=sQuery(id+"F26.wireOp",EDGE,"E21");var subQ2=sQuery(id+"F24.wireOp",EDGE,"E20");var subQ3=sQuery(id+"F22.wireOp",EDGE,"E19");var subQ4=sQuery(id+"F20.wireOp",EDGE,"E18");var subQ5=sQuery(id+"F0.wireOp",EDGE,"E0.sketch_text.stroke-101");var subQ6=sQuery(id+"F0.wireOp",EDGE,"E0.sketch_text.stroke-100");var subQ7=sQuery(id+"F0.wireOp",EDGE,"E0.sketch_text.stroke-99");Q0=makeQuery(id+"F31.boolean.opBoolean","MERGE",FACE,{"derivedFrom":[makeQuery(id+"F29.boolean.opBoolean","MERGE",FACE,{"derivedFrom":[makeQuery(id+"F27.boolean.opBoolean","MERGE",FACE,{"derivedFrom":[makeQuery(id+"F25.boolean.opBoolean","MERGE",FACE,{"derivedFrom":[makeQuery(id+"F23.boolean.opBoolean","MERGE",FACE,{"derivedFrom":[makeQuery(id+"F21.boolean.opBoolean","MERGE",FACE,{"derivedFrom":[makeQuery(id+"F1.opExtrude","CAP_FACE",FACE,{"disambiguationData":[OSD([sQuery(id+"F0.wireOp",EDGE,"E0.sketch_text.stroke-98"),subQ7,subQ6,subQ5])],"isStart":false}),makeQuery(id+"F21.opExtrude","CAP_FACE",FACE,{"disambiguationData":[OSD([subQ7,subQ6,subQ4])],"isStart":true})]}),makeQuery(id+"F23.opExtrude","CAP_FACE",FACE,{"disambiguationData":[OSD([subQ6,subQ5,subQ4,subQ3])],"isStart":true})]}),makeQuery(id+"F25.opExtrude","CAP_FACE",FACE,{"disambiguationData":[OSD([subQ4,subQ3,subQ2])],"isStart":true})]}),makeQuery(id+"F27.opExtrude","CAP_FACE",FACE,{"disambiguationData":[OSD([subQ3,subQ2,subQ1])],"isStart":true})]}),makeQuery(id+"F29.opExtrude","CAP_FACE",FACE,{"disambiguationData":[OSD([subQ2,subQ1,subQ0])],"isStart":true})]}),makeQuery(id+"F31.opExtrude","CAP_FACE",FACE,{"disambiguationData":[OSD([subQ0,sQuery(id+"F30.wireOp",EDGE,"E23"),sQuery(id+"F30.wireOp",EDGE,"E25")])],"isStart":true})]});}
            var sketch = newSketch(context, id + "F32", { "sketchPlane" : qUnion([Q0])});
            skLineSegment(sketch, "E26", {"start": v(-21.42, 15.45) * mm, "end": v(-19.41, 16.53) * mm});
            skLineSegment(sketch, "E27", {"start": v(-19.41, 16.53) * mm, "end": v(-20, 13.53) * mm});
            skLineSegment(sketch, "E28", {"start": v(-20, 13.53) * mm, "end": v(-21.42, 15.45) * mm});
            skSolve(sketch);
        }
        {
            var Q0;
            {var subQ0=sQuery(id+"F32.wireOp",EDGE,"E27");var subQ1=sQuery(id+"F32.wireOp",EDGE,"E26");var subQ2=makeQuery(id+"F32.imprint","INTERSECT",VERTEX,{"derivedFrom":[subQ1,subQ0]});Q0=makeQuery(id+"F32.imprint","IMPRINT",FACE,{"disambiguationData":[TD([[makeQuery(id+"F32.imprint","IMPRINT",EDGE,{"disambiguationData":[TD([[subQ2,1.0]])],"derivedFrom":subQ1}),-1.0]])]});}
            extrude(context, id + "F33", {"entities" : qUnion([Q0]), "operationType" : NewBodyOperationType.ADD, "oppositeDirection" : true, "depth" : 12.7 * mm, "offsetDistance" : 25.4 * mm});
        }
        {
            var Q0;
            {var subQ0=sQuery(id+"F26.wireOp",EDGE,"E21");var subQ1=sQuery(id+"F28.wireOp",EDGE,"E22");var subQ2=sQuery(id+"F24.wireOp",EDGE,"E20");var subQ3=sQuery(id+"F22.wireOp",EDGE,"E19");var subQ4=sQuery(id+"F20.wireOp",EDGE,"E18");var subQ5=sQuery(id+"F0.wireOp",EDGE,"E0.sketch_text.stroke-101");var subQ6=sQuery(id+"F0.wireOp",EDGE,"E0.sketch_text.stroke-100");var subQ7=sQuery(id+"F0.wireOp",EDGE,"E0.sketch_text.stroke-99");Q0=makeQuery(id+"F33.boolean.opBoolean","MERGE",FACE,{"derivedFrom":[makeQuery(id+"F31.boolean.opBoolean","MERGE",FACE,{"derivedFrom":[makeQuery(id+"F29.boolean.opBoolean","MERGE",FACE,{"derivedFrom":[makeQuery(id+"F27.boolean.opBoolean","MERGE",FACE,{"derivedFrom":[makeQuery(id+"F25.boolean.opBoolean","MERGE",FACE,{"derivedFrom":[makeQuery(id+"F23.boolean.opBoolean","MERGE",FACE,{"derivedFrom":[makeQuery(id+"F21.boolean.opBoolean","MERGE",FACE,{"derivedFrom":[makeQuery(id+"F1.opExtrude","CAP_FACE",FACE,{"disambiguationData":[OSD([sQuery(id+"F0.wireOp",EDGE,"E0.sketch_text.stroke-98"),subQ7,subQ6,subQ5])],"isStart":false}),makeQuery(id+"F21.opExtrude","CAP_FACE",FACE,{"disambiguationData":[OSD([subQ7,subQ6,subQ4])],"isStart":true})]}),makeQuery(id+"F23.opExtrude","CAP_FACE",FACE,{"disambiguationData":[OSD([subQ6,subQ5,subQ4,subQ3])],"isStart":true})]}),makeQuery(id+"F25.opExtrude","CAP_FACE",FACE,{"disambiguationData":[OSD([subQ4,subQ3,subQ2])],"isStart":true})]}),makeQuery(id+"F27.opExtrude","CAP_FACE",FACE,{"disambiguationData":[OSD([subQ3,subQ2,subQ0])],"isStart":true})]}),makeQuery(id+"F29.opExtrude","CAP_FACE",FACE,{"disambiguationData":[OSD([subQ2,subQ0,subQ1])],"isStart":true})]}),makeQuery(id+"F31.opExtrude","CAP_FACE",FACE,{"disambiguationData":[OSD([subQ1,sQuery(id+"F30.wireOp",EDGE,"E23"),sQuery(id+"F30.wireOp",EDGE,"E25")])],"isStart":true})]}),makeQuery(id+"F33.opExtrude","CAP_FACE",FACE,{"disambiguationData":[OSD([subQ0,sQuery(id+"F32.wireOp",EDGE,"E26"),sQuery(id+"F32.wireOp",EDGE,"E27")])],"isStart":true})]});}
            var sketch = newSketch(context, id + "F34", { "sketchPlane" : qUnion([Q0])});
            skLineSegment(sketch, "E29", {"start": v(-26.2, 15.29) * mm, "end": v(-25.82, 13.23) * mm});
            skLineSegment(sketch, "E30", {"start": v(-25.82, 13.23) * mm, "end": v(-24.38, 14.33) * mm});
            skLineSegment(sketch, "E31", {"start": v(-24.38, 14.33) * mm, "end": v(-26.2, 15.29) * mm});
            skSolve(sketch);
        }
        {
            var Q0;
            {var subQ0=sQuery(id+"F34.wireOp",EDGE,"E29");Q0=makeQuery(id+"F34.imprint","IMPRINT",FACE,{"disambiguationData":[TD([[makeQuery(id+"F34.imprint","IMPRINT",EDGE,{"derivedFrom":subQ0}),1.0]])]});}
            extrude(context, id + "F35", {"entities" : qUnion([Q0]), "operationType" : NewBodyOperationType.ADD, "oppositeDirection" : true, "depth" : 12.7 * mm, "offsetDistance" : 25.4 * mm});
        }
        {
            var Q0;
            {var subQ0=sQuery(id+"F24.wireOp",EDGE,"E20");var subQ1=sQuery(id+"F26.wireOp",EDGE,"E21");var subQ2=sQuery(id+"F28.wireOp",EDGE,"E22");var subQ3=sQuery(id+"F22.wireOp",EDGE,"E19");var subQ4=sQuery(id+"F20.wireOp",EDGE,"E18");var subQ5=sQuery(id+"F0.wireOp",EDGE,"E0.sketch_text.stroke-101");var subQ6=sQuery(id+"F0.wireOp",EDGE,"E0.sketch_text.stroke-100");var subQ7=sQuery(id+"F0.wireOp",EDGE,"E0.sketch_text.stroke-99");Q0=makeQuery(id+"F35.boolean.opBoolean","MERGE",FACE,{"derivedFrom":[makeQuery(id+"F33.boolean.opBoolean","MERGE",FACE,{"derivedFrom":[makeQuery(id+"F31.boolean.opBoolean","MERGE",FACE,{"derivedFrom":[makeQuery(id+"F29.boolean.opBoolean","MERGE",FACE,{"derivedFrom":[makeQuery(id+"F27.boolean.opBoolean","MERGE",FACE,{"derivedFrom":[makeQuery(id+"F25.boolean.opBoolean","MERGE",FACE,{"derivedFrom":[makeQuery(id+"F23.boolean.opBoolean","MERGE",FACE,{"derivedFrom":[makeQuery(id+"F21.boolean.opBoolean","MERGE",FACE,{"derivedFrom":[makeQuery(id+"F1.opExtrude","CAP_FACE",FACE,{"disambiguationData":[OSD([sQuery(id+"F0.wireOp",EDGE,"E0.sketch_text.stroke-98"),subQ7,subQ6,subQ5])],"isStart":false}),makeQuery(id+"F21.opExtrude","CAP_FACE",FACE,{"disambiguationData":[OSD([subQ7,subQ6,subQ4])],"isStart":true})]}),makeQuery(id+"F23.opExtrude","CAP_FACE",FACE,{"disambiguationData":[OSD([subQ6,subQ5,subQ4,subQ3])],"isStart":true})]}),makeQuery(id+"F25.opExtrude","CAP_FACE",FACE,{"disambiguationData":[OSD([subQ4,subQ3,subQ0])],"isStart":true})]}),makeQuery(id+"F27.opExtrude","CAP_FACE",FACE,{"disambiguationData":[OSD([subQ3,subQ0,subQ1])],"isStart":true})]}),makeQuery(id+"F29.opExtrude","CAP_FACE",FACE,{"disambiguationData":[OSD([subQ0,subQ1,subQ2])],"isStart":true})]}),makeQuery(id+"F31.opExtrude","CAP_FACE",FACE,{"disambiguationData":[OSD([subQ2,sQuery(id+"F30.wireOp",EDGE,"E23"),sQuery(id+"F30.wireOp",EDGE,"E25")])],"isStart":true})]}),makeQuery(id+"F33.opExtrude","CAP_FACE",FACE,{"disambiguationData":[OSD([subQ1,sQuery(id+"F32.wireOp",EDGE,"E26"),sQuery(id+"F32.wireOp",EDGE,"E27")])],"isStart":true})]}),makeQuery(id+"F35.opExtrude","CAP_FACE",FACE,{"disambiguationData":[OSD([subQ0,sQuery(id+"F34.wireOp",EDGE,"E29"),sQuery(id+"F34.wireOp",EDGE,"E31")])],"isStart":true})]});}
            var sketch = newSketch(context, id + "F36", { "sketchPlane" : qUnion([Q0])});
            skLineSegment(sketch, "E32", {"start": v(-19.56, 12.97) * mm, "end": v(-17.84, 13.53) * mm});
            skLineSegment(sketch, "E33", {"start": v(-17.84, 13.53) * mm, "end": v(-17.97, 11.43) * mm});
            skLineSegment(sketch, "E34", {"start": v(-17.97, 11.43) * mm, "end": v(-19.56, 12.97) * mm});
            skSolve(sketch);
        }
        {
            var Q0;
            {var subQ0=sQuery(id+"F36.wireOp",EDGE,"E33");var subQ1=sQuery(id+"F36.wireOp",EDGE,"E32");var subQ2=makeQuery(id+"F36.imprint","INTERSECT",VERTEX,{"derivedFrom":[subQ1,subQ0]});Q0=makeQuery(id+"F36.imprint","IMPRINT",FACE,{"disambiguationData":[TD([[makeQuery(id+"F36.imprint","IMPRINT",EDGE,{"disambiguationData":[TD([[subQ2,1.0]])],"derivedFrom":subQ1}),-1.0]])]});}
            extrude(context, id + "F37", {"entities" : qUnion([Q0]), "operationType" : NewBodyOperationType.ADD, "oppositeDirection" : true, "depth" : 12.7 * mm, "offsetDistance" : 25.4 * mm});
        }
        {
            var Q0;
            {var subQ0=sQuery(id+"F22.wireOp",EDGE,"E19");var subQ1=sQuery(id+"F24.wireOp",EDGE,"E20");var subQ2=sQuery(id+"F26.wireOp",EDGE,"E21");var subQ3=sQuery(id+"F28.wireOp",EDGE,"E22");var subQ4=sQuery(id+"F20.wireOp",EDGE,"E18");var subQ5=sQuery(id+"F0.wireOp",EDGE,"E0.sketch_text.stroke-101");var subQ6=sQuery(id+"F0.wireOp",EDGE,"E0.sketch_text.stroke-100");var subQ7=sQuery(id+"F0.wireOp",EDGE,"E0.sketch_text.stroke-99");Q0=makeQuery(id+"F37.boolean.opBoolean","MERGE",FACE,{"derivedFrom":[makeQuery(id+"F35.boolean.opBoolean","MERGE",FACE,{"derivedFrom":[makeQuery(id+"F33.boolean.opBoolean","MERGE",FACE,{"derivedFrom":[makeQuery(id+"F31.boolean.opBoolean","MERGE",FACE,{"derivedFrom":[makeQuery(id+"F29.boolean.opBoolean","MERGE",FACE,{"derivedFrom":[makeQuery(id+"F27.boolean.opBoolean","MERGE",FACE,{"derivedFrom":[makeQuery(id+"F25.boolean.opBoolean","MERGE",FACE,{"derivedFrom":[makeQuery(id+"F23.boolean.opBoolean","MERGE",FACE,{"derivedFrom":[makeQuery(id+"F21.boolean.opBoolean","MERGE",FACE,{"derivedFrom":[makeQuery(id+"F1.opExtrude","CAP_FACE",FACE,{"disambiguationData":[OSD([sQuery(id+"F0.wireOp",EDGE,"E0.sketch_text.stroke-98"),subQ7,subQ6,subQ5])],"isStart":false}),makeQuery(id+"F21.opExtrude","CAP_FACE",FACE,{"disambiguationData":[OSD([subQ7,subQ6,subQ4])],"isStart":true})]}),makeQuery(id+"F23.opExtrude","CAP_FACE",FACE,{"disambiguationData":[OSD([subQ6,subQ5,subQ4,subQ0])],"isStart":true})]}),makeQuery(id+"F25.opExtrude","CAP_FACE",FACE,{"disambiguationData":[OSD([subQ4,subQ0,subQ1])],"isStart":true})]}),makeQuery(id+"F27.opExtrude","CAP_FACE",FACE,{"disambiguationData":[OSD([subQ0,subQ1,subQ2])],"isStart":true})]}),makeQuery(id+"F29.opExtrude","CAP_FACE",FACE,{"disambiguationData":[OSD([subQ1,subQ2,subQ3])],"isStart":true})]}),makeQuery(id+"F31.opExtrude","CAP_FACE",FACE,{"disambiguationData":[OSD([subQ3,sQuery(id+"F30.wireOp",EDGE,"E23"),sQuery(id+"F30.wireOp",EDGE,"E25")])],"isStart":true})]}),makeQuery(id+"F33.opExtrude","CAP_FACE",FACE,{"disambiguationData":[OSD([subQ2,sQuery(id+"F32.wireOp",EDGE,"E26"),sQuery(id+"F32.wireOp",EDGE,"E27")])],"isStart":true})]}),makeQuery(id+"F35.opExtrude","CAP_FACE",FACE,{"disambiguationData":[OSD([subQ1,sQuery(id+"F34.wireOp",EDGE,"E29"),sQuery(id+"F34.wireOp",EDGE,"E31")])],"isStart":true})]}),makeQuery(id+"F37.opExtrude","CAP_FACE",FACE,{"disambiguationData":[OSD([subQ0,sQuery(id+"F36.wireOp",EDGE,"E32"),sQuery(id+"F36.wireOp",EDGE,"E33")])],"isStart":true})]});}
            var sketch = newSketch(context, id + "F38", { "sketchPlane" : qUnion([Q0])});
            skLineSegment(sketch, "E35", {"start": v(-25.7, 12.1) * mm, "end": v(-27.62, 12.9) * mm});
            skPoint(sketch, "E35.startSnap0", {"position": v(-26.98, 12.1) * mm});
            skLineSegment(sketch, "E36", {"start": v(-27.62, 12.9) * mm, "end": v(-27.26, 10.82) * mm});
            skLineSegment(sketch, "E37", {"start": v(-27.26, 10.82) * mm, "end": v(-25.7, 12.1) * mm});
            skSolve(sketch);
        }
        {
            var Q0;
            {var subQ0=sQuery(id+"F38.wireOp",EDGE,"E35");Q0=makeQuery(id+"F38.imprint","IMPRINT",FACE,{"disambiguationData":[TD([[makeQuery(id+"F38.imprint","IMPRINT",EDGE,{"derivedFrom":subQ0}),1.0]])]});}
            extrude(context, id + "F39", {"entities" : qUnion([Q0]), "operationType" : NewBodyOperationType.ADD, "oppositeDirection" : true, "depth" : 12.7 * mm, "offsetDistance" : 25.4 * mm});
        }
        {
            var Q0;
            {var subQ0=sQuery(id+"F20.wireOp",EDGE,"E18");var subQ1=sQuery(id+"F22.wireOp",EDGE,"E19");var subQ2=sQuery(id+"F24.wireOp",EDGE,"E20");var subQ3=sQuery(id+"F26.wireOp",EDGE,"E21");var subQ4=sQuery(id+"F28.wireOp",EDGE,"E22");var subQ5=sQuery(id+"F0.wireOp",EDGE,"E0.sketch_text.stroke-101");var subQ6=sQuery(id+"F0.wireOp",EDGE,"E0.sketch_text.stroke-100");var subQ7=sQuery(id+"F0.wireOp",EDGE,"E0.sketch_text.stroke-99");Q0=makeQuery(id+"F39.boolean.opBoolean","MERGE",FACE,{"derivedFrom":[makeQuery(id+"F37.boolean.opBoolean","MERGE",FACE,{"derivedFrom":[makeQuery(id+"F35.boolean.opBoolean","MERGE",FACE,{"derivedFrom":[makeQuery(id+"F33.boolean.opBoolean","MERGE",FACE,{"derivedFrom":[makeQuery(id+"F31.boolean.opBoolean","MERGE",FACE,{"derivedFrom":[makeQuery(id+"F29.boolean.opBoolean","MERGE",FACE,{"derivedFrom":[makeQuery(id+"F27.boolean.opBoolean","MERGE",FACE,{"derivedFrom":[makeQuery(id+"F25.boolean.opBoolean","MERGE",FACE,{"derivedFrom":[makeQuery(id+"F23.boolean.opBoolean","MERGE",FACE,{"derivedFrom":[makeQuery(id+"F21.boolean.opBoolean","MERGE",FACE,{"derivedFrom":[makeQuery(id+"F1.opExtrude","CAP_FACE",FACE,{"disambiguationData":[OSD([sQuery(id+"F0.wireOp",EDGE,"E0.sketch_text.stroke-98"),subQ7,subQ6,subQ5])],"isStart":false}),makeQuery(id+"F21.opExtrude","CAP_FACE",FACE,{"disambiguationData":[OSD([subQ7,subQ6,subQ0])],"isStart":true})]}),makeQuery(id+"F23.opExtrude","CAP_FACE",FACE,{"disambiguationData":[OSD([subQ6,subQ5,subQ0,subQ1])],"isStart":true})]}),makeQuery(id+"F25.opExtrude","CAP_FACE",FACE,{"disambiguationData":[OSD([subQ0,subQ1,subQ2])],"isStart":true})]}),makeQuery(id+"F27.opExtrude","CAP_FACE",FACE,{"disambiguationData":[OSD([subQ1,subQ2,subQ3])],"isStart":true})]}),makeQuery(id+"F29.opExtrude","CAP_FACE",FACE,{"disambiguationData":[OSD([subQ2,subQ3,subQ4])],"isStart":true})]}),makeQuery(id+"F31.opExtrude","CAP_FACE",FACE,{"disambiguationData":[OSD([subQ4,sQuery(id+"F30.wireOp",EDGE,"E23"),sQuery(id+"F30.wireOp",EDGE,"E25")])],"isStart":true})]}),makeQuery(id+"F33.opExtrude","CAP_FACE",FACE,{"disambiguationData":[OSD([subQ3,sQuery(id+"F32.wireOp",EDGE,"E26"),sQuery(id+"F32.wireOp",EDGE,"E27")])],"isStart":true})]}),makeQuery(id+"F35.opExtrude","CAP_FACE",FACE,{"disambiguationData":[OSD([subQ2,sQuery(id+"F34.wireOp",EDGE,"E29"),sQuery(id+"F34.wireOp",EDGE,"E31")])],"isStart":true})]}),makeQuery(id+"F37.opExtrude","CAP_FACE",FACE,{"disambiguationData":[OSD([subQ1,sQuery(id+"F36.wireOp",EDGE,"E32"),sQuery(id+"F36.wireOp",EDGE,"E33")])],"isStart":true})]}),makeQuery(id+"F39.opExtrude","CAP_FACE",FACE,{"disambiguationData":[OSD([subQ0,sQuery(id+"F38.wireOp",EDGE,"E35"),sQuery(id+"F38.wireOp",EDGE,"E36")])],"isStart":true})]});}
            var sketch = newSketch(context, id + "F40", { "sketchPlane" : qUnion([Q0])});
            skLineSegment(sketch, "E38.bottom", {"start": v(-24.24, 11.29) * mm, "end": v(-21.2, 11.29) * mm});
            skLineSegment(sketch, "E38.top", {"start": v(-24.24, 7.18) * mm, "end": v(-21.2, 7.18) * mm});
            skLineSegment(sketch, "E38.left", {"start": v(-24.24, 11.29) * mm, "end": v(-24.24, 7.18) * mm});
            skLineSegment(sketch, "E38.right", {"start": v(-21.2, 11.29) * mm, "end": v(-21.2, 7.18) * mm});
            skSolve(sketch);
        }
        {
            var Q0;
            Q0=makeQuery(id+"F40.imprint","IMPRINT",FACE,{"disambiguationData":[TD([[makeQuery(id+"F40.imprint","IMPRINT",EDGE,{"derivedFrom":sQuery(id+"F40.wireOp",EDGE,"E38.bottom")}),-1.0]])]});
            extrude(context, id + "F41", {"entities" : qUnion([Q0]), "operationType" : NewBodyOperationType.ADD, "oppositeDirection" : true, "depth" : 12.7 * mm, "offsetDistance" : 25.4 * mm});
        }
        {
            var Q0;
            Q0=makeQuery(id+"F1.opExtrude","CAP_FACE",FACE,{"disambiguationData":[OSD([sQuery(id+"F0.wireOp",EDGE,"E0.sketch_text.stroke-102"),sQuery(id+"F0.wireOp",EDGE,"E0.sketch_text.stroke-103"),sQuery(id+"F0.wireOp",EDGE,"E0.sketch_text.stroke-104"),sQuery(id+"F0.wireOp",EDGE,"E0.sketch_text.stroke-105"),sQuery(id+"F0.wireOp",EDGE,"E0.sketch_text.stroke-106"),sQuery(id+"F0.wireOp",EDGE,"E0.sketch_text.stroke-107"),sQuery(id+"F0.wireOp",EDGE,"E0.sketch_text.stroke-108"),sQuery(id+"F0.wireOp",EDGE,"E0.sketch_text.stroke-109"),sQuery(id+"F0.wireOp",EDGE,"E0.sketch_text.stroke-110"),sQuery(id+"F0.wireOp",EDGE,"E0.sketch_text.stroke-111"),sQuery(id+"F0.wireOp",EDGE,"E0.sketch_text.stroke-112"),sQuery(id+"F0.wireOp",EDGE,"E0.sketch_text.stroke-113"),sQuery(id+"F0.wireOp",EDGE,"E0.sketch_text.stroke-114"),sQuery(id+"F0.wireOp",EDGE,"E0.sketch_text.stroke-115"),sQuery(id+"F0.wireOp",EDGE,"E0.sketch_text.stroke-116"),sQuery(id+"F0.wireOp",EDGE,"E0.sketch_text.stroke-117"),sQuery(id+"F0.wireOp",EDGE,"E0.sketch_text.stroke-118"),sQuery(id+"F0.wireOp",EDGE,"E0.sketch_text.stroke-119"),sQuery(id+"F0.wireOp",EDGE,"E0.sketch_text.stroke-120")])],"isStart":false});
            var sketch = newSketch(context, id + "F42", { "sketchPlane" : qUnion([Q0])});
            skCircle(sketch, "E39", {"center": v(-13.1, -3.23) * mm, "radius": 7.08 * mm});
            skSolve(sketch);
        }
        {
            var Q0;
            Q0=makeQuery(id+"F42.imprint","IMPRINT",FACE,{"disambiguationData":[TD([[makeQuery(id+"F42.imprint","IMPRINT",EDGE,{"derivedFrom":sQuery(id+"F42.wireOp",EDGE,"E39")}),1.0]])]});
            extrude(context, id + "F43", {"entities" : qUnion([Q0]), "operationType" : NewBodyOperationType.ADD, "oppositeDirection" : true, "depth" : 12.7 * mm, "offsetDistance" : 25.4 * mm});
        }
        {
            var Q0;
            {var subQ0=sQuery(id+"F0.wireOp",EDGE,"E0.sketch_text.stroke-115");var subQ1=sQuery(id+"F0.wireOp",EDGE,"E0.sketch_text.stroke-114");var subQ2=sQuery(id+"F0.wireOp",EDGE,"E0.sketch_text.stroke-113");var subQ3=sQuery(id+"F0.wireOp",EDGE,"E0.sketch_text.stroke-112");var subQ4=sQuery(id+"F0.wireOp",EDGE,"E0.sketch_text.stroke-111");var subQ5=sQuery(id+"F0.wireOp",EDGE,"E0.sketch_text.stroke-110");var subQ6=sQuery(id+"F0.wireOp",EDGE,"E0.sketch_text.stroke-109");var subQ7=sQuery(id+"F0.wireOp",EDGE,"E0.sketch_text.stroke-108");var subQ8=sQuery(id+"F0.wireOp",EDGE,"E0.sketch_text.stroke-107");var subQ9=sQuery(id+"F0.wireOp",EDGE,"E0.sketch_text.stroke-106");var subQ10=sQuery(id+"F0.wireOp",EDGE,"E0.sketch_text.stroke-105");var subQ11=sQuery(id+"F0.wireOp",EDGE,"E0.sketch_text.stroke-104");var subQ12=sQuery(id+"F0.wireOp",EDGE,"E0.sketch_text.stroke-103");var subQ13=sQuery(id+"F0.wireOp",EDGE,"E0.sketch_text.stroke-102");Q0=makeQuery(id+"F43.boolean.opBoolean","MERGE",FACE,{"derivedFrom":[makeQuery(id+"F1.opExtrude","CAP_FACE",FACE,{"disambiguationData":[OSD([subQ13,subQ12,subQ11,subQ10,subQ9,subQ8,subQ7,subQ6,subQ5,subQ4,subQ3,subQ2,subQ1,subQ0,sQuery(id+"F0.wireOp",EDGE,"E0.sketch_text.stroke-116"),sQuery(id+"F0.wireOp",EDGE,"E0.sketch_text.stroke-117"),sQuery(id+"F0.wireOp",EDGE,"E0.sketch_text.stroke-118"),sQuery(id+"F0.wireOp",EDGE,"E0.sketch_text.stroke-119"),sQuery(id+"F0.wireOp",EDGE,"E0.sketch_text.stroke-120")])],"isStart":false}),makeQuery(id+"F43.opExtrude","CAP_FACE",FACE,{"disambiguationData":[OSD([subQ13,subQ12,subQ11,subQ10,subQ9,subQ8,subQ7,subQ6,subQ5,subQ4,subQ3,subQ2,subQ1,subQ0,sQuery(id+"F42.wireOp",EDGE,"E39")])],"isStart":true})]});}
            var sketch = newSketch(context, id + "F44", { "sketchPlane" : qUnion([Q0])});
            skCircle(sketch, "E40", {"center": v(-13.42, -0.9) * mm, "radius": 3.74 * mm});
            skSolve(sketch);
        }
        {
            var Q0;
            Q0=makeQuery(id+"F44.imprint","IMPRINT",FACE,{"disambiguationData":[TD([[makeQuery(id+"F44.imprint","IMPRINT",EDGE,{"derivedFrom":makeQuery(id+"F1.opExtrude","CAP_EDGE",EDGE,{"disambiguationData":[OSD([sQuery(id+"F0.wireOp",EDGE,"E0.sketch_text.stroke-116")])],"isStart":false})}),1.0]])]});
            extrude(context, id + "F45", {"entities" : qUnion([Q0]), "operationType" : NewBodyOperationType.ADD, "oppositeDirection" : true, "depth" : 12.7 * mm, "offsetDistance" : 25.4 * mm});
        }
        {
            var Q0;
            {var subQ0=sQuery(id+"F0.wireOp",EDGE,"E0.sketch_text.stroke-120");var subQ1=sQuery(id+"F0.wireOp",EDGE,"E0.sketch_text.stroke-119");var subQ2=sQuery(id+"F0.wireOp",EDGE,"E0.sketch_text.stroke-118");var subQ3=sQuery(id+"F0.wireOp",EDGE,"E0.sketch_text.stroke-117");var subQ4=sQuery(id+"F0.wireOp",EDGE,"E0.sketch_text.stroke-116");var subQ5=sQuery(id+"F0.wireOp",EDGE,"E0.sketch_text.stroke-115");var subQ6=sQuery(id+"F0.wireOp",EDGE,"E0.sketch_text.stroke-114");var subQ7=sQuery(id+"F0.wireOp",EDGE,"E0.sketch_text.stroke-113");var subQ8=sQuery(id+"F0.wireOp",EDGE,"E0.sketch_text.stroke-112");var subQ9=sQuery(id+"F0.wireOp",EDGE,"E0.sketch_text.stroke-111");var subQ10=sQuery(id+"F0.wireOp",EDGE,"E0.sketch_text.stroke-110");var subQ11=sQuery(id+"F0.wireOp",EDGE,"E0.sketch_text.stroke-109");var subQ12=sQuery(id+"F0.wireOp",EDGE,"E0.sketch_text.stroke-108");var subQ13=sQuery(id+"F0.wireOp",EDGE,"E0.sketch_text.stroke-107");var subQ14=sQuery(id+"F0.wireOp",EDGE,"E0.sketch_text.stroke-106");var subQ15=sQuery(id+"F0.wireOp",EDGE,"E0.sketch_text.stroke-105");var subQ16=sQuery(id+"F0.wireOp",EDGE,"E0.sketch_text.stroke-104");var subQ17=sQuery(id+"F0.wireOp",EDGE,"E0.sketch_text.stroke-103");var subQ18=sQuery(id+"F0.wireOp",EDGE,"E0.sketch_text.stroke-102");Q0=makeQuery(id+"F45.boolean.opBoolean","MERGE",FACE,{"derivedFrom":[makeQuery(id+"F43.boolean.opBoolean","MERGE",FACE,{"derivedFrom":[makeQuery(id+"F1.opExtrude","CAP_FACE",FACE,{"disambiguationData":[OSD([subQ18,subQ17,subQ16,subQ15,subQ14,subQ13,subQ12,subQ11,subQ10,subQ9,subQ8,subQ7,subQ6,subQ5,subQ4,subQ3,subQ2,subQ1,subQ0])],"isStart":false}),makeQuery(id+"F43.opExtrude","CAP_FACE",FACE,{"disambiguationData":[OSD([subQ18,subQ17,subQ16,subQ15,subQ14,subQ13,subQ12,subQ11,subQ10,subQ9,subQ8,subQ7,subQ6,subQ5,sQuery(id+"F42.wireOp",EDGE,"E39")])],"isStart":true})]}),makeQuery(id+"F45.opExtrude","CAP_FACE",FACE,{"disambiguationData":[OSD([subQ4,subQ3,subQ2,subQ1,subQ0])],"isStart":true})]});}
            var sketch = newSketch(context, id + "F46", { "sketchPlane" : qUnion([Q0])});
            skArc(sketch, "E41", {"start": v(-8.16, -1.13) * mm, "mid": v(-15.3, 1.8) * mm, "end": v(-18.1, -5.4) * mm});
            skSolve(sketch);
        }
        {
            var Q0;
            Q0=sQuery(id+"F46.wireOp",EDGE,"E41");
            extrude(context, id + "F47", {"bodyType" : ToolBodyType.SURFACE, "surfaceEntities" : qUnion([Q0]), "oppositeDirection" : true, "depth" : 12.7 * mm, "offsetDistance" : 25.4 * mm});
        }
        {
            var Q0;
            {var subQ0=sQuery(id+"F0.wireOp",EDGE,"E0.sketch_text.stroke-120");var subQ1=sQuery(id+"F0.wireOp",EDGE,"E0.sketch_text.stroke-119");var subQ2=sQuery(id+"F0.wireOp",EDGE,"E0.sketch_text.stroke-118");var subQ3=sQuery(id+"F0.wireOp",EDGE,"E0.sketch_text.stroke-117");var subQ4=sQuery(id+"F0.wireOp",EDGE,"E0.sketch_text.stroke-116");var subQ5=sQuery(id+"F0.wireOp",EDGE,"E0.sketch_text.stroke-115");var subQ6=sQuery(id+"F0.wireOp",EDGE,"E0.sketch_text.stroke-114");var subQ7=sQuery(id+"F0.wireOp",EDGE,"E0.sketch_text.stroke-113");var subQ8=sQuery(id+"F0.wireOp",EDGE,"E0.sketch_text.stroke-112");var subQ9=sQuery(id+"F0.wireOp",EDGE,"E0.sketch_text.stroke-111");var subQ10=sQuery(id+"F0.wireOp",EDGE,"E0.sketch_text.stroke-110");var subQ11=sQuery(id+"F0.wireOp",EDGE,"E0.sketch_text.stroke-109");var subQ12=sQuery(id+"F0.wireOp",EDGE,"E0.sketch_text.stroke-108");var subQ13=sQuery(id+"F0.wireOp",EDGE,"E0.sketch_text.stroke-107");var subQ14=sQuery(id+"F0.wireOp",EDGE,"E0.sketch_text.stroke-106");var subQ15=sQuery(id+"F0.wireOp",EDGE,"E0.sketch_text.stroke-105");var subQ16=sQuery(id+"F0.wireOp",EDGE,"E0.sketch_text.stroke-104");var subQ17=sQuery(id+"F0.wireOp",EDGE,"E0.sketch_text.stroke-103");var subQ18=sQuery(id+"F0.wireOp",EDGE,"E0.sketch_text.stroke-102");Q0=makeQuery(id+"F45.boolean.opBoolean","MERGE",FACE,{"derivedFrom":[makeQuery(id+"F43.boolean.opBoolean","MERGE",FACE,{"derivedFrom":[makeQuery(id+"F1.opExtrude","CAP_FACE",FACE,{"disambiguationData":[OSD([subQ18,subQ17,subQ16,subQ15,subQ14,subQ13,subQ12,subQ11,subQ10,subQ9,subQ8,subQ7,subQ6,subQ5,subQ4,subQ3,subQ2,subQ1,subQ0])],"isStart":false}),makeQuery(id+"F43.opExtrude","CAP_FACE",FACE,{"disambiguationData":[OSD([subQ18,subQ17,subQ16,subQ15,subQ14,subQ13,subQ12,subQ11,subQ10,subQ9,subQ8,subQ7,subQ6,subQ5,sQuery(id+"F42.wireOp",EDGE,"E39")])],"isStart":true})]}),makeQuery(id+"F45.opExtrude","CAP_FACE",FACE,{"disambiguationData":[OSD([subQ4,subQ3,subQ2,subQ1,subQ0])],"isStart":true})]});}
            var sketch = newSketch(context, id + "F48", { "sketchPlane" : qUnion([Q0])});
            skLineSegment(sketch, "E42", {"start": v(-18.1, -5.37) * mm, "end": v(-8.15, -1.13) * mm});
            skLineSegment(sketch, "E43", {"start": v(-8.15, -1.13) * mm, "end": v(-18.1, -5.37) * mm});
            skSolve(sketch);
        }
        {
            var Q0;
            Q0=sQuery(id+"F48.wireOp",EDGE,"E42");
            extrude(context, id + "F49", {"bodyType" : ToolBodyType.SURFACE, "surfaceEntities" : qUnion([Q0]), "oppositeDirection" : true, "depth" : 12.7 * mm, "offsetDistance" : 25.4 * mm});
        }
        {
            var Q0;
            {var subQ0=sQuery(id+"F0.wireOp",EDGE,"E0.sketch_text.stroke-120");var subQ1=sQuery(id+"F0.wireOp",EDGE,"E0.sketch_text.stroke-119");var subQ2=sQuery(id+"F0.wireOp",EDGE,"E0.sketch_text.stroke-118");var subQ3=sQuery(id+"F0.wireOp",EDGE,"E0.sketch_text.stroke-117");var subQ4=sQuery(id+"F0.wireOp",EDGE,"E0.sketch_text.stroke-116");var subQ5=sQuery(id+"F0.wireOp",EDGE,"E0.sketch_text.stroke-115");var subQ6=sQuery(id+"F0.wireOp",EDGE,"E0.sketch_text.stroke-114");var subQ7=sQuery(id+"F0.wireOp",EDGE,"E0.sketch_text.stroke-113");var subQ8=sQuery(id+"F0.wireOp",EDGE,"E0.sketch_text.stroke-112");var subQ9=sQuery(id+"F0.wireOp",EDGE,"E0.sketch_text.stroke-111");var subQ10=sQuery(id+"F0.wireOp",EDGE,"E0.sketch_text.stroke-110");var subQ11=sQuery(id+"F0.wireOp",EDGE,"E0.sketch_text.stroke-109");var subQ12=sQuery(id+"F0.wireOp",EDGE,"E0.sketch_text.stroke-108");var subQ13=sQuery(id+"F0.wireOp",EDGE,"E0.sketch_text.stroke-107");var subQ14=sQuery(id+"F0.wireOp",EDGE,"E0.sketch_text.stroke-106");var subQ15=sQuery(id+"F0.wireOp",EDGE,"E0.sketch_text.stroke-105");var subQ16=sQuery(id+"F0.wireOp",EDGE,"E0.sketch_text.stroke-104");var subQ17=sQuery(id+"F0.wireOp",EDGE,"E0.sketch_text.stroke-103");var subQ18=sQuery(id+"F0.wireOp",EDGE,"E0.sketch_text.stroke-102");Q0=makeQuery(id+"F45.boolean.opBoolean","MERGE",FACE,{"derivedFrom":[makeQuery(id+"F43.boolean.opBoolean","MERGE",FACE,{"derivedFrom":[makeQuery(id+"F1.opExtrude","CAP_FACE",FACE,{"disambiguationData":[OSD([subQ18,subQ17,subQ16,subQ15,subQ14,subQ13,subQ12,subQ11,subQ10,subQ9,subQ8,subQ7,subQ6,subQ5,subQ4,subQ3,subQ2,subQ1,subQ0])],"isStart":false}),makeQuery(id+"F43.opExtrude","CAP_FACE",FACE,{"disambiguationData":[OSD([subQ18,subQ17,subQ16,subQ15,subQ14,subQ13,subQ12,subQ11,subQ10,subQ9,subQ8,subQ7,subQ6,subQ5,sQuery(id+"F42.wireOp",EDGE,"E39")])],"isStart":true})]}),makeQuery(id+"F45.opExtrude","CAP_FACE",FACE,{"disambiguationData":[OSD([subQ4,subQ3,subQ2,subQ1,subQ0])],"isStart":true})]});}
            var sketch = newSketch(context, id + "F50", { "sketchPlane" : qUnion([Q0])});
            skArc(sketch, "E44", {"start": v(-17.87, -5.82) * mm, "mid": v(-10.77, -8.6) * mm, "end": v(-7.95, -1.52) * mm});
            skSolve(sketch);
        }
        {
            var Q0;
            Q0=sQuery(id+"F50.wireOp",EDGE,"E44");
            extrude(context, id + "F51", {"bodyType" : ToolBodyType.SURFACE, "surfaceEntities" : qUnion([Q0]), "oppositeDirection" : true, "depth" : 12.7 * mm, "offsetDistance" : 25.4 * mm});
        }
        {
            var Q0;
            {var subQ0=sQuery(id+"F0.wireOp",EDGE,"E0.sketch_text.stroke-120");var subQ1=sQuery(id+"F0.wireOp",EDGE,"E0.sketch_text.stroke-119");var subQ2=sQuery(id+"F0.wireOp",EDGE,"E0.sketch_text.stroke-118");var subQ3=sQuery(id+"F0.wireOp",EDGE,"E0.sketch_text.stroke-117");var subQ4=sQuery(id+"F0.wireOp",EDGE,"E0.sketch_text.stroke-116");var subQ5=sQuery(id+"F0.wireOp",EDGE,"E0.sketch_text.stroke-115");var subQ6=sQuery(id+"F0.wireOp",EDGE,"E0.sketch_text.stroke-114");var subQ7=sQuery(id+"F0.wireOp",EDGE,"E0.sketch_text.stroke-113");var subQ8=sQuery(id+"F0.wireOp",EDGE,"E0.sketch_text.stroke-112");var subQ9=sQuery(id+"F0.wireOp",EDGE,"E0.sketch_text.stroke-111");var subQ10=sQuery(id+"F0.wireOp",EDGE,"E0.sketch_text.stroke-110");var subQ11=sQuery(id+"F0.wireOp",EDGE,"E0.sketch_text.stroke-109");var subQ12=sQuery(id+"F0.wireOp",EDGE,"E0.sketch_text.stroke-108");var subQ13=sQuery(id+"F0.wireOp",EDGE,"E0.sketch_text.stroke-107");var subQ14=sQuery(id+"F0.wireOp",EDGE,"E0.sketch_text.stroke-106");var subQ15=sQuery(id+"F0.wireOp",EDGE,"E0.sketch_text.stroke-105");var subQ16=sQuery(id+"F0.wireOp",EDGE,"E0.sketch_text.stroke-104");var subQ17=sQuery(id+"F0.wireOp",EDGE,"E0.sketch_text.stroke-103");var subQ18=sQuery(id+"F0.wireOp",EDGE,"E0.sketch_text.stroke-102");Q0=makeQuery(id+"F45.boolean.opBoolean","MERGE",FACE,{"derivedFrom":[makeQuery(id+"F43.boolean.opBoolean","MERGE",FACE,{"derivedFrom":[makeQuery(id+"F1.opExtrude","CAP_FACE",FACE,{"disambiguationData":[OSD([subQ18,subQ17,subQ16,subQ15,subQ14,subQ13,subQ12,subQ11,subQ10,subQ9,subQ8,subQ7,subQ6,subQ5,subQ4,subQ3,subQ2,subQ1,subQ0])],"isStart":false}),makeQuery(id+"F43.opExtrude","CAP_FACE",FACE,{"disambiguationData":[OSD([subQ18,subQ17,subQ16,subQ15,subQ14,subQ13,subQ12,subQ11,subQ10,subQ9,subQ8,subQ7,subQ6,subQ5,sQuery(id+"F42.wireOp",EDGE,"E39")])],"isStart":true})]}),makeQuery(id+"F45.opExtrude","CAP_FACE",FACE,{"disambiguationData":[OSD([subQ4,subQ3,subQ2,subQ1,subQ0])],"isStart":true})]});}
            var sketch = newSketch(context, id + "F52", { "sketchPlane" : qUnion([Q0])});
            skLineSegment(sketch, "E45", {"start": v(-17.86, -5.81) * mm, "end": v(-7.94, -1.52) * mm});
            skLineSegment(sketch, "E46", {"start": v(-7.94, -1.52) * mm, "end": v(-17.86, -5.81) * mm});
            skSolve(sketch);
        }
        {
            var Q0;
            Q0=sQuery(id+"F52.wireOp",EDGE,"E45");
            extrude(context, id + "F53", {"bodyType" : ToolBodyType.SURFACE, "surfaceEntities" : qUnion([Q0]), "oppositeDirection" : true, "depth" : 12.7 * mm, "offsetDistance" : 25.4 * mm});
        }
        {
            var Q0;
            Q0=makeQuery(id+"F19.opExtrude","CAP_FACE",FACE,{"disambiguationData":[OSD([sQuery(id+"F0.wireOp",EDGE,"E0.sketch_text.stroke-29"),sQuery(id+"F0.wireOp",EDGE,"E0.sketch_text.stroke-30"),sQuery(id+"F0.wireOp",EDGE,"E0.sketch_text.stroke-31"),sQuery(id+"F0.wireOp",EDGE,"E0.sketch_text.stroke-32"),sQuery(id+"F0.wireOp",EDGE,"E0.sketch_text.stroke-33"),sQuery(id+"F0.wireOp",EDGE,"E0.sketch_text.stroke-34"),sQuery(id+"F0.wireOp",EDGE,"E0.sketch_text.stroke-35"),sQuery(id+"F0.wireOp",EDGE,"E0.sketch_text.stroke-36")])],"isStart":true});
            var sketch = newSketch(context, id + "F54", { "sketchPlane" : qUnion([Q0])});
            skSolve(sketch);
        }
        {
            var Q0;
            Q0=makeQuery(id+"F54.imprint","IMPRINT",FACE,{"disambiguationData":[TD([[makeQuery(id+"F54.imprint","IMPRINT",EDGE,{"derivedFrom":makeQuery(id+"F19.opExtrude","CAP_EDGE",EDGE,{"disambiguationData":[OSD([sQuery(id+"F0.wireOp",EDGE,"E0.sketch_text.stroke-29")])],"isStart":true})}),1.0]])]});
            extrude(context, id + "F55", {"entities" : qUnion([Q0]), "operationType" : NewBodyOperationType.ADD, "oppositeDirection" : true, "depth" : 12.7 * mm, "offsetDistance" : 25.4 * mm});
        }
    });
